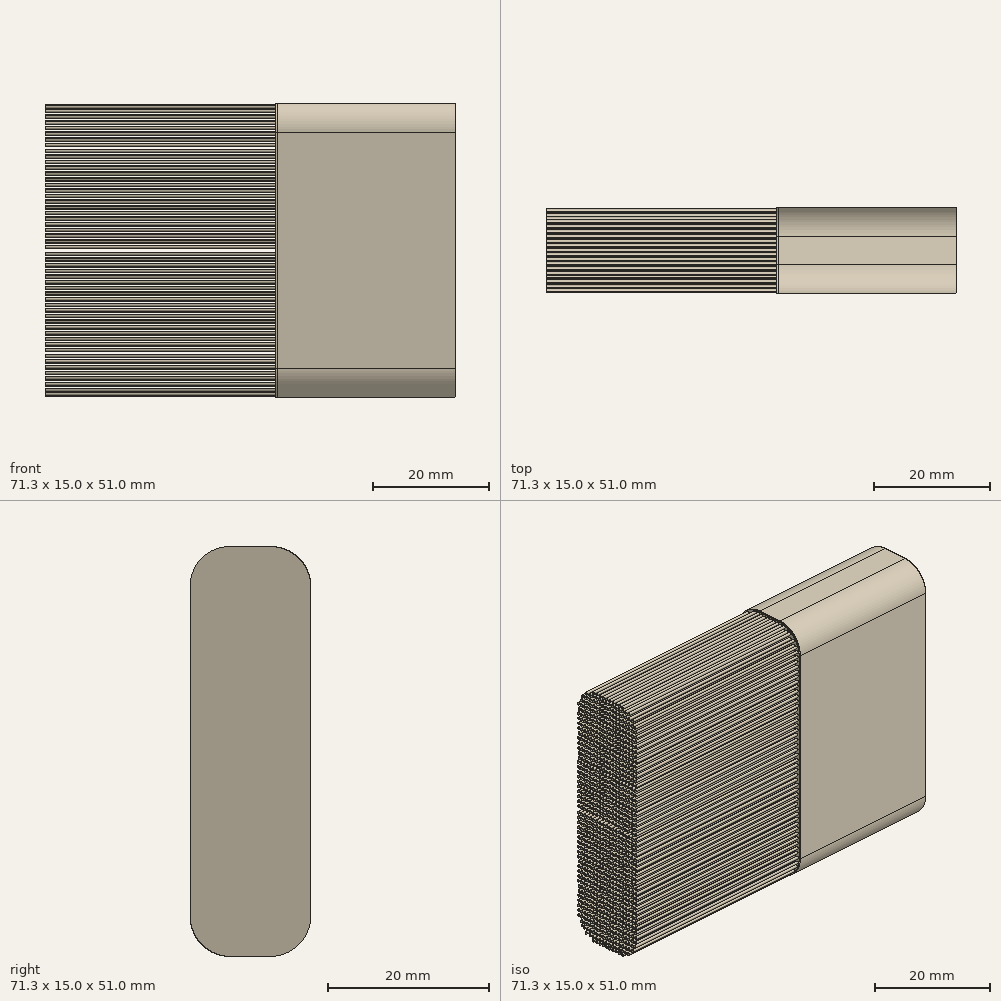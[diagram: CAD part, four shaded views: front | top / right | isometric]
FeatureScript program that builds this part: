
annotation { "Feature Type Name" : "Feature", "Feature Type Description" : "" }
export const myFeature = defineFeature(function(context is Context, id is Id, definition is map)
    precondition{}
    {
        {
            var Q0;
            Q0=qCreatedBy(makeId("Front.planeOp"),FACE);
            var sketch = newSketch(context, id + "F0", { "sketchPlane" : qUnion([Q0])});
            skLineSegment(sketch, "E0.bottom", {"start": v(15.5, -25.5) * mm, "end": v(-15.5, -25.5) * mm});
            skLineSegment(sketch, "E0.top", {"start": v(15.5, 25.5) * mm, "end": v(-15.5, 25.5) * mm});
            skLineSegment(sketch, "E0.left", {"start": v(15.5, -25.5) * mm, "end": v(15.5, 25.5) * mm});
            skLineSegment(sketch, "E0.right", {"start": v(-15.5, -25.5) * mm, "end": v(-15.5, 25.5) * mm});
            skPoint(sketch, "E0.middle", {"position": v(0, 0) * mm});
            skSolve(sketch);
        }
        {
            var Q0;
            Q0=makeQuery(id+"F0.imprint","IMPRINT",FACE,{"disambiguationData":[TD([[makeQuery(id+"F0.imprint","IMPRINT",EDGE,{"derivedFrom":sQuery(id+"F0.wireOp",EDGE,"E0.bottom")}),-1.0]])]});
            extrude(context, id + "F1", {"entities" : qUnion([Q0]), "depth" : 15 * mm});
        }
        {
            var Q0;
            Q0=makeQuery(id+"F1.opExtrude","CAP_EDGE",EDGE,{"disambiguationData":[OSD([sQuery(id+"F0.wireOp",EDGE,"E0.top")])],"isStart":true});
            var Q1;
            Q1=makeQuery(id+"F1.opExtrude","CAP_EDGE",EDGE,{"disambiguationData":[OSD([sQuery(id+"F0.wireOp",EDGE,"E0.bottom")])],"isStart":true});
            var Q2;
            Q2=makeQuery(id+"F1.opExtrude","CAP_EDGE",EDGE,{"disambiguationData":[OSD([sQuery(id+"F0.wireOp",EDGE,"E0.bottom")])],"isStart":false});
            var Q3;
            Q3=makeQuery(id+"F1.opExtrude","CAP_EDGE",EDGE,{"disambiguationData":[OSD([sQuery(id+"F0.wireOp",EDGE,"E0.top")])],"isStart":false});
            fillet(context, id + "F2", {"entities" : qUnion([Q0, Q1, Q2, Q3]), "radius" : 5 * mm, "tangentPropagation" : true, "allowEdgeOverflow" : false});
        }
        {
            var Q0;
            Q0=qCreatedBy(makeId("Right.planeOp"),FACE);
            cPlane(context, id + "F3", {"entities" : qUnion([Q0]), "cplaneType" : CPlaneType.OFFSET, "offset" : 15.8 * mm, "oppositeDirection" : true, "width" : 150 * mm, "height" : 150 * mm});
        }
        {
            var Q0;
            Q0=qCreatedBy(id+"F3.planeOp",FACE);
            var sketch = newSketch(context, id + "F4", { "sketchPlane" : qUnion([Q0])});
            skLineSegment(sketch, "E1.0.0", {"start": v(-10, 25.5) * mm, "end": v(-5, 25.5) * mm});
            skArc(sketch, "E1.0.1", {"start": v(-5, 25.5) * mm, "mid": v(-1.46, 24.04) * mm, "end": v(0, 20.5) * mm});
            skLineSegment(sketch, "E1.0.2", {"start": v(0, 20.5) * mm, "end": v(0, -20.5) * mm});
            skArc(sketch, "E1.0.3", {"start": v(0, -20.5) * mm, "mid": v(-1.46, -24.04) * mm, "end": v(-5, -25.5) * mm});
            skLineSegment(sketch, "E1.0.4", {"start": v(-5, -25.5) * mm, "end": v(-10, -25.5) * mm});
            skArc(sketch, "E1.0.5", {"start": v(-10, -25.5) * mm, "mid": v(-13.54, -24.04) * mm, "end": v(-15, -20.5) * mm});
            skLineSegment(sketch, "E1.0.6", {"start": v(-15, -20.5) * mm, "end": v(-15, 20.5) * mm});
            skArc(sketch, "E1.0.7", {"start": v(-15, 20.5) * mm, "mid": v(-13.54, 24.04) * mm, "end": v(-10, 25.5) * mm});
            skSolve(sketch);
        }
        {
            var Q0;
            Q0=makeQuery(id+"F4.imprint","IMPRINT",FACE,{"disambiguationData":[TD([[makeQuery(id+"F4.imprint","IMPRINT",EDGE,{"derivedFrom":sQuery(id+"F4.wireOp",EDGE,"E1.0.0")}),-1.0]])]});
            extrude(context, id + "F5", {"entities" : qUnion([Q0]), "depth" : 0.3 * mm});
        }
        {
            var Q0;
            Q0=makeQuery(id+"F4.imprint","IMPRINT",FACE,{"disambiguationData":[TD([[makeQuery(id+"F4.imprint","IMPRINT",EDGE,{"derivedFrom":sQuery(id+"F4.wireOp",EDGE,"E1.0.0")}),-1.0]])]});
            var sketch = newSketch(context, id + "F6", { "sketchPlane" : qUnion([Q0])});
            skCircle(sketch, "E2", {"center": v(-8.78, 4.59) * mm, "radius": 0.25 * mm});
            skCircle(sketch, "E3", {"center": v(-9.57, 4.53) * mm, "radius": 0.25 * mm});
            skCircle(sketch, "E4", {"center": v(-10.4, 4.5) * mm, "radius": 0.25 * mm});
            skCircle(sketch, "E5", {"center": v(-11.22, 4.53) * mm, "radius": 0.25 * mm});
            skCircle(sketch, "E6", {"center": v(-8, 4.59) * mm, "radius": 0.25 * mm});
            skCircle(sketch, "E7", {"center": v(-13.64, 4.5) * mm, "radius": 0.25 * mm});
            skCircle(sketch, "E8", {"center": v(-11.98, 4.56) * mm, "radius": 0.25 * mm});
            skCircle(sketch, "E9", {"center": v(-14.45, 4.53) * mm, "radius": 0.25 * mm});
            skCircle(sketch, "E10", {"center": v(-0.37, 4.62) * mm, "radius": 0.25 * mm});
            skCircle(sketch, "E11", {"center": v(-12.74, 4.5) * mm, "radius": 0.25 * mm});
            skCircle(sketch, "E12", {"center": v(-6.43, 4.55) * mm, "radius": 0.25 * mm});
            skCircle(sketch, "E13", {"center": v(-5.64, 4.6) * mm, "radius": 0.25 * mm});
            skCircle(sketch, "E14", {"center": v(-4.8, 4.63) * mm, "radius": 0.25 * mm});
            skCircle(sketch, "E15", {"center": v(-3.99, 4.6) * mm, "radius": 0.25 * mm});
            skCircle(sketch, "E16", {"center": v(-7.22, 4.55) * mm, "radius": 0.25 * mm});
            skCircle(sketch, "E17", {"center": v(-1.78, 4.61) * mm, "radius": 0.25 * mm});
            skCircle(sketch, "E18", {"center": v(-3.23, 4.58) * mm, "radius": 0.25 * mm});
            skCircle(sketch, "E19", {"center": v(-1.03, 4.63) * mm, "radius": 0.25 * mm});
            skCircle(sketch, "E20", {"center": v(-2.47, 4.63) * mm, "radius": 0.25 * mm});
            skCircle(sketch, "E21", {"center": v(-8.86, 3.61) * mm, "radius": 0.25 * mm});
            skCircle(sketch, "E22", {"center": v(-9.64, 3.56) * mm, "radius": 0.25 * mm});
            skCircle(sketch, "E23", {"center": v(-10.48, 3.53) * mm, "radius": 0.25 * mm});
            skCircle(sketch, "E24", {"center": v(-11.3, 3.56) * mm, "radius": 0.25 * mm});
            skCircle(sketch, "E25", {"center": v(-8.07, 3.61) * mm, "radius": 0.25 * mm});
            skCircle(sketch, "E26", {"center": v(-13.71, 3.53) * mm, "radius": 0.25 * mm});
            skCircle(sketch, "E27", {"center": v(-12.06, 3.59) * mm, "radius": 0.25 * mm});
            skCircle(sketch, "E28", {"center": v(-14.52, 3.56) * mm, "radius": 0.25 * mm});
            skCircle(sketch, "E29", {"center": v(-0.44, 3.65) * mm, "radius": 0.25 * mm});
            skCircle(sketch, "E30", {"center": v(-12.82, 3.53) * mm, "radius": 0.25 * mm});
            skCircle(sketch, "E31", {"center": v(-6.5, 3.58) * mm, "radius": 0.25 * mm});
            skCircle(sketch, "E32", {"center": v(-5.72, 3.63) * mm, "radius": 0.25 * mm});
            skCircle(sketch, "E33", {"center": v(-4.88, 3.66) * mm, "radius": 0.25 * mm});
            skCircle(sketch, "E34", {"center": v(-4.06, 3.63) * mm, "radius": 0.25 * mm});
            skCircle(sketch, "E35", {"center": v(-7.3, 3.58) * mm, "radius": 0.25 * mm});
            skCircle(sketch, "E36", {"center": v(-1.86, 3.64) * mm, "radius": 0.25 * mm});
            skCircle(sketch, "E37", {"center": v(-3.3, 3.6) * mm, "radius": 0.25 * mm});
            skCircle(sketch, "E38", {"center": v(-1.1, 3.66) * mm, "radius": 0.25 * mm});
            skCircle(sketch, "E39", {"center": v(-2.54, 3.66) * mm, "radius": 0.25 * mm});
            skCircle(sketch, "E40", {"center": v(-8.86, 2.59) * mm, "radius": 0.25 * mm});
            skCircle(sketch, "E41", {"center": v(-9.64, 2.54) * mm, "radius": 0.25 * mm});
            skCircle(sketch, "E42", {"center": v(-10.48, 2.51) * mm, "radius": 0.25 * mm});
            skCircle(sketch, "E43", {"center": v(-11.3, 2.54) * mm, "radius": 0.25 * mm});
            skCircle(sketch, "E44", {"center": v(-8.07, 2.59) * mm, "radius": 0.25 * mm});
            skCircle(sketch, "E45", {"center": v(-13.71, 2.51) * mm, "radius": 0.25 * mm});
            skCircle(sketch, "E46", {"center": v(-12.06, 2.56) * mm, "radius": 0.25 * mm});
            skCircle(sketch, "E47", {"center": v(-14.52, 2.54) * mm, "radius": 0.25 * mm});
            skCircle(sketch, "E48", {"center": v(-0.44, 2.63) * mm, "radius": 0.25 * mm});
            skCircle(sketch, "E49", {"center": v(-12.82, 2.51) * mm, "radius": 0.25 * mm});
            skCircle(sketch, "E50", {"center": v(-6.5, 2.56) * mm, "radius": 0.25 * mm});
            skCircle(sketch, "E51", {"center": v(-5.72, 2.6) * mm, "radius": 0.25 * mm});
            skCircle(sketch, "E52", {"center": v(-4.88, 2.64) * mm, "radius": 0.25 * mm});
            skCircle(sketch, "E53", {"center": v(-4.06, 2.6) * mm, "radius": 0.25 * mm});
            skCircle(sketch, "E54", {"center": v(-7.3, 2.56) * mm, "radius": 0.25 * mm});
            skCircle(sketch, "E55", {"center": v(-1.86, 2.62) * mm, "radius": 0.25 * mm});
            skCircle(sketch, "E56", {"center": v(-3.3, 2.58) * mm, "radius": 0.25 * mm});
            skCircle(sketch, "E57", {"center": v(-1.1, 2.64) * mm, "radius": 0.25 * mm});
            skCircle(sketch, "E58", {"center": v(-2.54, 2.64) * mm, "radius": 0.25 * mm});
            skCircle(sketch, "E59", {"center": v(-8.86, 1.62) * mm, "radius": 0.25 * mm});
            skCircle(sketch, "E60", {"center": v(-9.64, 1.56) * mm, "radius": 0.25 * mm});
            skCircle(sketch, "E61", {"center": v(-10.48, 1.54) * mm, "radius": 0.25 * mm});
            skCircle(sketch, "E62", {"center": v(-11.3, 1.56) * mm, "radius": 0.25 * mm});
            skCircle(sketch, "E63", {"center": v(-8.07, 1.62) * mm, "radius": 0.25 * mm});
            skCircle(sketch, "E64", {"center": v(-13.71, 1.54) * mm, "radius": 0.25 * mm});
            skCircle(sketch, "E65", {"center": v(-12.06, 1.6) * mm, "radius": 0.25 * mm});
            skCircle(sketch, "E66", {"center": v(-14.52, 1.56) * mm, "radius": 0.25 * mm});
            skCircle(sketch, "E67", {"center": v(-0.44, 1.65) * mm, "radius": 0.25 * mm});
            skCircle(sketch, "E68", {"center": v(-12.82, 1.54) * mm, "radius": 0.25 * mm});
            skCircle(sketch, "E69", {"center": v(-6.5, 1.58) * mm, "radius": 0.25 * mm});
            skCircle(sketch, "E70", {"center": v(-5.72, 1.64) * mm, "radius": 0.25 * mm});
            skCircle(sketch, "E71", {"center": v(-4.88, 1.66) * mm, "radius": 0.25 * mm});
            skCircle(sketch, "E72", {"center": v(-4.06, 1.64) * mm, "radius": 0.25 * mm});
            skCircle(sketch, "E73", {"center": v(-7.3, 1.58) * mm, "radius": 0.25 * mm});
            skCircle(sketch, "E74", {"center": v(-1.86, 1.64) * mm, "radius": 0.25 * mm});
            skCircle(sketch, "E75", {"center": v(-3.3, 1.61) * mm, "radius": 0.25 * mm});
            skCircle(sketch, "E76", {"center": v(-1.1, 1.66) * mm, "radius": 0.25 * mm});
            skCircle(sketch, "E77", {"center": v(-2.54, 1.66) * mm, "radius": 0.25 * mm});
            skCircle(sketch, "E78", {"center": v(-8.9, 0.62) * mm, "radius": 0.25 * mm});
            skCircle(sketch, "E79", {"center": v(-9.69, 0.57) * mm, "radius": 0.25 * mm});
            skCircle(sketch, "E80", {"center": v(-10.52, 0.54) * mm, "radius": 0.25 * mm});
            skCircle(sketch, "E81", {"center": v(-11.34, 0.57) * mm, "radius": 0.25 * mm});
            skCircle(sketch, "E82", {"center": v(-8.11, 0.62) * mm, "radius": 0.25 * mm});
            skCircle(sketch, "E83", {"center": v(-13.75, 0.54) * mm, "radius": 0.25 * mm});
            skCircle(sketch, "E84", {"center": v(-12.1, 0.6) * mm, "radius": 0.25 * mm});
            skCircle(sketch, "E85", {"center": v(-14.57, 0.57) * mm, "radius": 0.25 * mm});
            skCircle(sketch, "E86", {"center": v(-0.49, 0.66) * mm, "radius": 0.25 * mm});
            skCircle(sketch, "E87", {"center": v(-12.86, 0.54) * mm, "radius": 0.25 * mm});
            skCircle(sketch, "E88", {"center": v(-6.55, 0.6) * mm, "radius": 0.25 * mm});
            skCircle(sketch, "E89", {"center": v(-5.76, 0.64) * mm, "radius": 0.25 * mm});
            skCircle(sketch, "E90", {"center": v(-4.92, 0.67) * mm, "radius": 0.25 * mm});
            skCircle(sketch, "E91", {"center": v(-4.1, 0.64) * mm, "radius": 0.25 * mm});
            skCircle(sketch, "E92", {"center": v(-7.33, 0.6) * mm, "radius": 0.25 * mm});
            skCircle(sketch, "E93", {"center": v(-1.9, 0.65) * mm, "radius": 0.25 * mm});
            skCircle(sketch, "E94", {"center": v(-3.34, 0.62) * mm, "radius": 0.25 * mm});
            skCircle(sketch, "E95", {"center": v(-1.14, 0.67) * mm, "radius": 0.25 * mm});
            skCircle(sketch, "E96", {"center": v(-2.58, 0.67) * mm, "radius": 0.25 * mm});
            skCircle(sketch, "E97", {"center": v(-8.78, 9.52) * mm, "radius": 0.25 * mm});
            skCircle(sketch, "E98", {"center": v(-9.57, 9.47) * mm, "radius": 0.25 * mm});
            skCircle(sketch, "E99", {"center": v(-10.4, 9.44) * mm, "radius": 0.25 * mm});
            skCircle(sketch, "E100", {"center": v(-11.22, 9.47) * mm, "radius": 0.25 * mm});
            skCircle(sketch, "E101", {"center": v(-8, 9.52) * mm, "radius": 0.25 * mm});
            skCircle(sketch, "E102", {"center": v(-13.64, 9.44) * mm, "radius": 0.25 * mm});
            skCircle(sketch, "E103", {"center": v(-11.98, 9.5) * mm, "radius": 0.25 * mm});
            skCircle(sketch, "E104", {"center": v(-14.45, 9.47) * mm, "radius": 0.25 * mm});
            skCircle(sketch, "E105", {"center": v(-0.37, 9.56) * mm, "radius": 0.25 * mm});
            skCircle(sketch, "E106", {"center": v(-12.74, 9.44) * mm, "radius": 0.25 * mm});
            skCircle(sketch, "E107", {"center": v(-6.43, 9.5) * mm, "radius": 0.25 * mm});
            skCircle(sketch, "E108", {"center": v(-5.64, 9.54) * mm, "radius": 0.25 * mm});
            skCircle(sketch, "E109", {"center": v(-4.8, 9.57) * mm, "radius": 0.25 * mm});
            skCircle(sketch, "E110", {"center": v(-3.99, 9.54) * mm, "radius": 0.25 * mm});
            skCircle(sketch, "E111", {"center": v(-7.22, 9.5) * mm, "radius": 0.25 * mm});
            skCircle(sketch, "E112", {"center": v(-1.78, 9.55) * mm, "radius": 0.25 * mm});
            skCircle(sketch, "E113", {"center": v(-3.23, 9.52) * mm, "radius": 0.25 * mm});
            skCircle(sketch, "E114", {"center": v(-1.03, 9.57) * mm, "radius": 0.25 * mm});
            skCircle(sketch, "E115", {"center": v(-2.47, 9.57) * mm, "radius": 0.25 * mm});
            skCircle(sketch, "E116", {"center": v(-8.86, 8.55) * mm, "radius": 0.25 * mm});
            skCircle(sketch, "E117", {"center": v(-9.64, 8.5) * mm, "radius": 0.25 * mm});
            skCircle(sketch, "E118", {"center": v(-10.48, 8.47) * mm, "radius": 0.25 * mm});
            skCircle(sketch, "E119", {"center": v(-11.3, 8.5) * mm, "radius": 0.25 * mm});
            skCircle(sketch, "E120", {"center": v(-8.07, 8.55) * mm, "radius": 0.25 * mm});
            skCircle(sketch, "E121", {"center": v(-13.71, 8.47) * mm, "radius": 0.25 * mm});
            skCircle(sketch, "E122", {"center": v(-12.06, 8.52) * mm, "radius": 0.25 * mm});
            skCircle(sketch, "E123", {"center": v(-14.52, 8.5) * mm, "radius": 0.25 * mm});
            skCircle(sketch, "E124", {"center": v(-0.44, 8.59) * mm, "radius": 0.25 * mm});
            skCircle(sketch, "E125", {"center": v(-12.82, 8.47) * mm, "radius": 0.25 * mm});
            skCircle(sketch, "E126", {"center": v(-6.5, 8.52) * mm, "radius": 0.25 * mm});
            skCircle(sketch, "E127", {"center": v(-5.72, 8.57) * mm, "radius": 0.25 * mm});
            skCircle(sketch, "E128", {"center": v(-4.88, 8.6) * mm, "radius": 0.25 * mm});
            skCircle(sketch, "E129", {"center": v(-4.06, 8.57) * mm, "radius": 0.25 * mm});
            skCircle(sketch, "E130", {"center": v(-7.3, 8.52) * mm, "radius": 0.25 * mm});
            skCircle(sketch, "E131", {"center": v(-1.86, 8.58) * mm, "radius": 0.25 * mm});
            skCircle(sketch, "E132", {"center": v(-3.3, 8.54) * mm, "radius": 0.25 * mm});
            skCircle(sketch, "E133", {"center": v(-1.1, 8.6) * mm, "radius": 0.25 * mm});
            skCircle(sketch, "E134", {"center": v(-2.54, 8.6) * mm, "radius": 0.25 * mm});
            skCircle(sketch, "E135", {"center": v(-8.86, 7.53) * mm, "radius": 0.25 * mm});
            skCircle(sketch, "E136", {"center": v(-9.64, 7.47) * mm, "radius": 0.25 * mm});
            skCircle(sketch, "E137", {"center": v(-10.48, 7.45) * mm, "radius": 0.25 * mm});
            skCircle(sketch, "E138", {"center": v(-11.3, 7.47) * mm, "radius": 0.25 * mm});
            skCircle(sketch, "E139", {"center": v(-8.07, 7.53) * mm, "radius": 0.25 * mm});
            skCircle(sketch, "E140", {"center": v(-13.71, 7.45) * mm, "radius": 0.25 * mm});
            skCircle(sketch, "E141", {"center": v(-12.06, 7.5) * mm, "radius": 0.25 * mm});
            skCircle(sketch, "E142", {"center": v(-14.52, 7.47) * mm, "radius": 0.25 * mm});
            skCircle(sketch, "E143", {"center": v(-0.44, 7.56) * mm, "radius": 0.25 * mm});
            skCircle(sketch, "E144", {"center": v(-12.82, 7.45) * mm, "radius": 0.25 * mm});
            skCircle(sketch, "E145", {"center": v(-6.5, 7.5) * mm, "radius": 0.25 * mm});
            skCircle(sketch, "E146", {"center": v(-5.72, 7.55) * mm, "radius": 0.25 * mm});
            skCircle(sketch, "E147", {"center": v(-4.88, 7.57) * mm, "radius": 0.25 * mm});
            skCircle(sketch, "E148", {"center": v(-4.06, 7.55) * mm, "radius": 0.25 * mm});
            skCircle(sketch, "E149", {"center": v(-7.3, 7.5) * mm, "radius": 0.25 * mm});
            skCircle(sketch, "E150", {"center": v(-1.86, 7.55) * mm, "radius": 0.25 * mm});
            skCircle(sketch, "E151", {"center": v(-3.3, 7.52) * mm, "radius": 0.25 * mm});
            skCircle(sketch, "E152", {"center": v(-1.1, 7.57) * mm, "radius": 0.25 * mm});
            skCircle(sketch, "E153", {"center": v(-2.54, 7.57) * mm, "radius": 0.25 * mm});
            skCircle(sketch, "E154", {"center": v(-8.86, 6.55) * mm, "radius": 0.25 * mm});
            skCircle(sketch, "E155", {"center": v(-9.64, 6.5) * mm, "radius": 0.25 * mm});
            skCircle(sketch, "E156", {"center": v(-10.48, 6.47) * mm, "radius": 0.25 * mm});
            skCircle(sketch, "E157", {"center": v(-11.3, 6.5) * mm, "radius": 0.25 * mm});
            skCircle(sketch, "E158", {"center": v(-8.07, 6.55) * mm, "radius": 0.25 * mm});
            skCircle(sketch, "E159", {"center": v(-13.71, 6.47) * mm, "radius": 0.25 * mm});
            skCircle(sketch, "E160", {"center": v(-12.06, 6.53) * mm, "radius": 0.25 * mm});
            skCircle(sketch, "E161", {"center": v(-14.52, 6.5) * mm, "radius": 0.25 * mm});
            skCircle(sketch, "E162", {"center": v(-0.44, 6.6) * mm, "radius": 0.25 * mm});
            skCircle(sketch, "E163", {"center": v(-12.82, 6.47) * mm, "radius": 0.25 * mm});
            skCircle(sketch, "E164", {"center": v(-6.5, 6.52) * mm, "radius": 0.25 * mm});
            skCircle(sketch, "E165", {"center": v(-5.72, 6.57) * mm, "radius": 0.25 * mm});
            skCircle(sketch, "E166", {"center": v(-4.88, 6.6) * mm, "radius": 0.25 * mm});
            skCircle(sketch, "E167", {"center": v(-4.06, 6.57) * mm, "radius": 0.25 * mm});
            skCircle(sketch, "E168", {"center": v(-7.3, 6.52) * mm, "radius": 0.25 * mm});
            skCircle(sketch, "E169", {"center": v(-1.86, 6.58) * mm, "radius": 0.25 * mm});
            skCircle(sketch, "E170", {"center": v(-3.3, 6.55) * mm, "radius": 0.25 * mm});
            skCircle(sketch, "E171", {"center": v(-1.1, 6.6) * mm, "radius": 0.25 * mm});
            skCircle(sketch, "E172", {"center": v(-2.54, 6.6) * mm, "radius": 0.25 * mm});
            skCircle(sketch, "E173", {"center": v(-8.9, 5.56) * mm, "radius": 0.25 * mm});
            skCircle(sketch, "E174", {"center": v(-9.69, 5.5) * mm, "radius": 0.25 * mm});
            skCircle(sketch, "E175", {"center": v(-10.52, 5.48) * mm, "radius": 0.25 * mm});
            skCircle(sketch, "E176", {"center": v(-11.34, 5.5) * mm, "radius": 0.25 * mm});
            skCircle(sketch, "E177", {"center": v(-8.11, 5.56) * mm, "radius": 0.25 * mm});
            skCircle(sketch, "E178", {"center": v(-13.75, 5.48) * mm, "radius": 0.25 * mm});
            skCircle(sketch, "E179", {"center": v(-12.1, 5.53) * mm, "radius": 0.25 * mm});
            skCircle(sketch, "E180", {"center": v(-14.57, 5.5) * mm, "radius": 0.25 * mm});
            skCircle(sketch, "E181", {"center": v(-0.49, 5.6) * mm, "radius": 0.25 * mm});
            skCircle(sketch, "E182", {"center": v(-12.86, 5.48) * mm, "radius": 0.25 * mm});
            skCircle(sketch, "E183", {"center": v(-6.55, 5.53) * mm, "radius": 0.25 * mm});
            skCircle(sketch, "E184", {"center": v(-5.76, 5.58) * mm, "radius": 0.25 * mm});
            skCircle(sketch, "E185", {"center": v(-4.92, 5.6) * mm, "radius": 0.25 * mm});
            skCircle(sketch, "E186", {"center": v(-4.1, 5.58) * mm, "radius": 0.25 * mm});
            skCircle(sketch, "E187", {"center": v(-7.33, 5.53) * mm, "radius": 0.25 * mm});
            skCircle(sketch, "E188", {"center": v(-1.9, 5.59) * mm, "radius": 0.25 * mm});
            skCircle(sketch, "E189", {"center": v(-3.34, 5.55) * mm, "radius": 0.25 * mm});
            skCircle(sketch, "E190", {"center": v(-1.14, 5.6) * mm, "radius": 0.25 * mm});
            skCircle(sketch, "E191", {"center": v(-2.58, 5.6) * mm, "radius": 0.25 * mm});
            skCircle(sketch, "E192", {"center": v(-8.86, 14.4) * mm, "radius": 0.25 * mm});
            skCircle(sketch, "E193", {"center": v(-9.64, 14.35) * mm, "radius": 0.25 * mm});
            skCircle(sketch, "E194", {"center": v(-10.48, 14.32) * mm, "radius": 0.25 * mm});
            skCircle(sketch, "E195", {"center": v(-11.3, 14.35) * mm, "radius": 0.25 * mm});
            skCircle(sketch, "E196", {"center": v(-8.07, 14.4) * mm, "radius": 0.25 * mm});
            skCircle(sketch, "E197", {"center": v(-13.71, 14.32) * mm, "radius": 0.25 * mm});
            skCircle(sketch, "E198", {"center": v(-12.06, 14.38) * mm, "radius": 0.25 * mm});
            skCircle(sketch, "E199", {"center": v(-14.52, 14.35) * mm, "radius": 0.25 * mm});
            skCircle(sketch, "E200", {"center": v(-0.44, 14.44) * mm, "radius": 0.25 * mm});
            skCircle(sketch, "E201", {"center": v(-12.82, 14.32) * mm, "radius": 0.25 * mm});
            skCircle(sketch, "E202", {"center": v(-6.5, 14.37) * mm, "radius": 0.25 * mm});
            skCircle(sketch, "E203", {"center": v(-5.72, 14.42) * mm, "radius": 0.25 * mm});
            skCircle(sketch, "E204", {"center": v(-4.88, 14.45) * mm, "radius": 0.25 * mm});
            skCircle(sketch, "E205", {"center": v(-4.06, 14.42) * mm, "radius": 0.25 * mm});
            skCircle(sketch, "E206", {"center": v(-7.3, 14.37) * mm, "radius": 0.25 * mm});
            skCircle(sketch, "E207", {"center": v(-1.86, 14.43) * mm, "radius": 0.25 * mm});
            skCircle(sketch, "E208", {"center": v(-3.3, 14.4) * mm, "radius": 0.25 * mm});
            skCircle(sketch, "E209", {"center": v(-1.1, 14.45) * mm, "radius": 0.25 * mm});
            skCircle(sketch, "E210", {"center": v(-2.54, 14.45) * mm, "radius": 0.25 * mm});
            skCircle(sketch, "E211", {"center": v(-8.93, 13.43) * mm, "radius": 0.25 * mm});
            skCircle(sketch, "E212", {"center": v(-9.72, 13.38) * mm, "radius": 0.25 * mm});
            skCircle(sketch, "E213", {"center": v(-10.56, 13.35) * mm, "radius": 0.25 * mm});
            skCircle(sketch, "E214", {"center": v(-11.37, 13.38) * mm, "radius": 0.25 * mm});
            skCircle(sketch, "E215", {"center": v(-8.14, 13.43) * mm, "radius": 0.25 * mm});
            skCircle(sketch, "E216", {"center": v(-13.79, 13.35) * mm, "radius": 0.25 * mm});
            skCircle(sketch, "E217", {"center": v(-12.13, 13.4) * mm, "radius": 0.25 * mm});
            skCircle(sketch, "E218", {"center": v(-14.6, 13.38) * mm, "radius": 0.25 * mm});
            skCircle(sketch, "E219", {"center": v(-0.52, 13.46) * mm, "radius": 0.25 * mm});
            skCircle(sketch, "E220", {"center": v(-12.9, 13.35) * mm, "radius": 0.25 * mm});
            skCircle(sketch, "E221", {"center": v(-6.58, 13.4) * mm, "radius": 0.25 * mm});
            skCircle(sketch, "E222", {"center": v(-5.8, 13.45) * mm, "radius": 0.25 * mm});
            skCircle(sketch, "E223", {"center": v(-4.95, 13.47) * mm, "radius": 0.25 * mm});
            skCircle(sketch, "E224", {"center": v(-4.14, 13.45) * mm, "radius": 0.25 * mm});
            skCircle(sketch, "E225", {"center": v(-7.37, 13.4) * mm, "radius": 0.25 * mm});
            skCircle(sketch, "E226", {"center": v(-1.93, 13.46) * mm, "radius": 0.25 * mm});
            skCircle(sketch, "E227", {"center": v(-3.38, 13.42) * mm, "radius": 0.25 * mm});
            skCircle(sketch, "E228", {"center": v(-1.18, 13.47) * mm, "radius": 0.25 * mm});
            skCircle(sketch, "E229", {"center": v(-2.62, 13.47) * mm, "radius": 0.25 * mm});
            skCircle(sketch, "E230", {"center": v(-8.93, 12.4) * mm, "radius": 0.25 * mm});
            skCircle(sketch, "E231", {"center": v(-9.72, 12.35) * mm, "radius": 0.25 * mm});
            skCircle(sketch, "E232", {"center": v(-10.56, 12.33) * mm, "radius": 0.25 * mm});
            skCircle(sketch, "E233", {"center": v(-11.37, 12.35) * mm, "radius": 0.25 * mm});
            skCircle(sketch, "E234", {"center": v(-8.14, 12.4) * mm, "radius": 0.25 * mm});
            skCircle(sketch, "E235", {"center": v(-13.79, 12.33) * mm, "radius": 0.25 * mm});
            skCircle(sketch, "E236", {"center": v(-12.13, 12.38) * mm, "radius": 0.25 * mm});
            skCircle(sketch, "E237", {"center": v(-14.6, 12.35) * mm, "radius": 0.25 * mm});
            skCircle(sketch, "E238", {"center": v(-0.52, 12.44) * mm, "radius": 0.25 * mm});
            skCircle(sketch, "E239", {"center": v(-12.9, 12.33) * mm, "radius": 0.25 * mm});
            skCircle(sketch, "E240", {"center": v(-6.58, 12.37) * mm, "radius": 0.25 * mm});
            skCircle(sketch, "E241", {"center": v(-5.8, 12.43) * mm, "radius": 0.25 * mm});
            skCircle(sketch, "E242", {"center": v(-4.95, 12.45) * mm, "radius": 0.25 * mm});
            skCircle(sketch, "E243", {"center": v(-4.14, 12.43) * mm, "radius": 0.25 * mm});
            skCircle(sketch, "E244", {"center": v(-7.37, 12.37) * mm, "radius": 0.25 * mm});
            skCircle(sketch, "E245", {"center": v(-1.93, 12.43) * mm, "radius": 0.25 * mm});
            skCircle(sketch, "E246", {"center": v(-3.38, 12.4) * mm, "radius": 0.25 * mm});
            skCircle(sketch, "E247", {"center": v(-1.18, 12.45) * mm, "radius": 0.25 * mm});
            skCircle(sketch, "E248", {"center": v(-2.62, 12.45) * mm, "radius": 0.25 * mm});
            skCircle(sketch, "E249", {"center": v(-8.93, 11.43) * mm, "radius": 0.25 * mm});
            skCircle(sketch, "E250", {"center": v(-9.72, 11.38) * mm, "radius": 0.25 * mm});
            skCircle(sketch, "E251", {"center": v(-10.56, 11.35) * mm, "radius": 0.25 * mm});
            skCircle(sketch, "E252", {"center": v(-11.37, 11.38) * mm, "radius": 0.25 * mm});
            skCircle(sketch, "E253", {"center": v(-8.14, 11.43) * mm, "radius": 0.25 * mm});
            skCircle(sketch, "E254", {"center": v(-13.79, 11.35) * mm, "radius": 0.25 * mm});
            skCircle(sketch, "E255", {"center": v(-12.13, 11.4) * mm, "radius": 0.25 * mm});
            skCircle(sketch, "E256", {"center": v(-14.6, 11.38) * mm, "radius": 0.25 * mm});
            skCircle(sketch, "E257", {"center": v(-0.52, 11.47) * mm, "radius": 0.25 * mm});
            skCircle(sketch, "E258", {"center": v(-12.9, 11.35) * mm, "radius": 0.25 * mm});
            skCircle(sketch, "E259", {"center": v(-6.58, 11.4) * mm, "radius": 0.25 * mm});
            skCircle(sketch, "E260", {"center": v(-5.8, 11.45) * mm, "radius": 0.25 * mm});
            skCircle(sketch, "E261", {"center": v(-4.95, 11.48) * mm, "radius": 0.25 * mm});
            skCircle(sketch, "E262", {"center": v(-4.14, 11.45) * mm, "radius": 0.25 * mm});
            skCircle(sketch, "E263", {"center": v(-7.37, 11.4) * mm, "radius": 0.25 * mm});
            skCircle(sketch, "E264", {"center": v(-1.93, 11.46) * mm, "radius": 0.25 * mm});
            skCircle(sketch, "E265", {"center": v(-3.38, 11.43) * mm, "radius": 0.25 * mm});
            skCircle(sketch, "E266", {"center": v(-1.18, 11.48) * mm, "radius": 0.25 * mm});
            skCircle(sketch, "E267", {"center": v(-2.62, 11.48) * mm, "radius": 0.25 * mm});
            skCircle(sketch, "E268", {"center": v(-8.97, 10.44) * mm, "radius": 0.25 * mm});
            skCircle(sketch, "E269", {"center": v(-9.76, 10.39) * mm, "radius": 0.25 * mm});
            skCircle(sketch, "E270", {"center": v(-10.6, 10.36) * mm, "radius": 0.25 * mm});
            skCircle(sketch, "E271", {"center": v(-11.41, 10.39) * mm, "radius": 0.25 * mm});
            skCircle(sketch, "E272", {"center": v(-8.19, 10.44) * mm, "radius": 0.25 * mm});
            skCircle(sketch, "E273", {"center": v(-13.83, 10.36) * mm, "radius": 0.25 * mm});
            skCircle(sketch, "E274", {"center": v(-12.17, 10.41) * mm, "radius": 0.25 * mm});
            skCircle(sketch, "E275", {"center": v(-14.64, 10.39) * mm, "radius": 0.25 * mm});
            skCircle(sketch, "E276", {"center": v(-0.56, 10.48) * mm, "radius": 0.25 * mm});
            skCircle(sketch, "E277", {"center": v(-12.94, 10.36) * mm, "radius": 0.25 * mm});
            skCircle(sketch, "E278", {"center": v(-6.62, 10.4) * mm, "radius": 0.25 * mm});
            skCircle(sketch, "E279", {"center": v(-5.83, 10.46) * mm, "radius": 0.25 * mm});
            skCircle(sketch, "E280", {"center": v(-5, 10.49) * mm, "radius": 0.25 * mm});
            skCircle(sketch, "E281", {"center": v(-4.18, 10.46) * mm, "radius": 0.25 * mm});
            skCircle(sketch, "E282", {"center": v(-7.4, 10.4) * mm, "radius": 0.25 * mm});
            skCircle(sketch, "E283", {"center": v(-1.98, 10.47) * mm, "radius": 0.25 * mm});
            skCircle(sketch, "E284", {"center": v(-3.42, 10.43) * mm, "radius": 0.25 * mm});
            skCircle(sketch, "E285", {"center": v(-1.22, 10.49) * mm, "radius": 0.25 * mm});
            skCircle(sketch, "E286", {"center": v(-2.66, 10.49) * mm, "radius": 0.25 * mm});
            skCircle(sketch, "E287", {"center": v(-8.86, 19.34) * mm, "radius": 0.25 * mm});
            skCircle(sketch, "E288", {"center": v(-9.64, 19.29) * mm, "radius": 0.25 * mm});
            skCircle(sketch, "E289", {"center": v(-10.48, 19.26) * mm, "radius": 0.25 * mm});
            skCircle(sketch, "E290", {"center": v(-11.3, 19.29) * mm, "radius": 0.25 * mm});
            skCircle(sketch, "E291", {"center": v(-8.07, 19.34) * mm, "radius": 0.25 * mm});
            skCircle(sketch, "E292", {"center": v(-13.71, 19.26) * mm, "radius": 0.25 * mm});
            skCircle(sketch, "E293", {"center": v(-12.06, 19.31) * mm, "radius": 0.25 * mm});
            skCircle(sketch, "E294", {"center": v(-14.52, 19.29) * mm, "radius": 0.25 * mm});
            skCircle(sketch, "E295", {"center": v(-0.44, 19.38) * mm, "radius": 0.25 * mm});
            skCircle(sketch, "E296", {"center": v(-12.82, 19.26) * mm, "radius": 0.25 * mm});
            skCircle(sketch, "E297", {"center": v(-6.5, 19.3) * mm, "radius": 0.25 * mm});
            skCircle(sketch, "E298", {"center": v(-5.72, 19.36) * mm, "radius": 0.25 * mm});
            skCircle(sketch, "E299", {"center": v(-4.88, 19.39) * mm, "radius": 0.25 * mm});
            skCircle(sketch, "E300", {"center": v(-4.06, 19.36) * mm, "radius": 0.25 * mm});
            skCircle(sketch, "E301", {"center": v(-7.3, 19.3) * mm, "radius": 0.25 * mm});
            skCircle(sketch, "E302", {"center": v(-1.86, 19.37) * mm, "radius": 0.25 * mm});
            skCircle(sketch, "E303", {"center": v(-3.3, 19.33) * mm, "radius": 0.25 * mm});
            skCircle(sketch, "E304", {"center": v(-1.1, 19.39) * mm, "radius": 0.25 * mm});
            skCircle(sketch, "E305", {"center": v(-2.54, 19.39) * mm, "radius": 0.25 * mm});
            skCircle(sketch, "E306", {"center": v(-8.93, 18.36) * mm, "radius": 0.25 * mm});
            skCircle(sketch, "E307", {"center": v(-9.72, 18.31) * mm, "radius": 0.25 * mm});
            skCircle(sketch, "E308", {"center": v(-10.56, 18.29) * mm, "radius": 0.25 * mm});
            skCircle(sketch, "E309", {"center": v(-11.37, 18.31) * mm, "radius": 0.25 * mm});
            skCircle(sketch, "E310", {"center": v(-8.14, 18.36) * mm, "radius": 0.25 * mm});
            skCircle(sketch, "E311", {"center": v(-13.79, 18.29) * mm, "radius": 0.25 * mm});
            skCircle(sketch, "E312", {"center": v(-12.13, 18.34) * mm, "radius": 0.25 * mm});
            skCircle(sketch, "E313", {"center": v(-14.6, 18.31) * mm, "radius": 0.25 * mm});
            skCircle(sketch, "E314", {"center": v(-0.52, 18.4) * mm, "radius": 0.25 * mm});
            skCircle(sketch, "E315", {"center": v(-12.9, 18.29) * mm, "radius": 0.25 * mm});
            skCircle(sketch, "E316", {"center": v(-6.58, 18.33) * mm, "radius": 0.25 * mm});
            skCircle(sketch, "E317", {"center": v(-5.8, 18.38) * mm, "radius": 0.25 * mm});
            skCircle(sketch, "E318", {"center": v(-4.95, 18.41) * mm, "radius": 0.25 * mm});
            skCircle(sketch, "E319", {"center": v(-4.14, 18.38) * mm, "radius": 0.25 * mm});
            skCircle(sketch, "E320", {"center": v(-7.37, 18.33) * mm, "radius": 0.25 * mm});
            skCircle(sketch, "E321", {"center": v(-1.93, 18.4) * mm, "radius": 0.25 * mm});
            skCircle(sketch, "E322", {"center": v(-3.38, 18.36) * mm, "radius": 0.25 * mm});
            skCircle(sketch, "E323", {"center": v(-1.18, 18.41) * mm, "radius": 0.25 * mm});
            skCircle(sketch, "E324", {"center": v(-2.62, 18.41) * mm, "radius": 0.25 * mm});
            skCircle(sketch, "E325", {"center": v(-8.93, 17.34) * mm, "radius": 0.25 * mm});
            skCircle(sketch, "E326", {"center": v(-9.72, 17.29) * mm, "radius": 0.25 * mm});
            skCircle(sketch, "E327", {"center": v(-10.56, 17.26) * mm, "radius": 0.25 * mm});
            skCircle(sketch, "E328", {"center": v(-11.37, 17.29) * mm, "radius": 0.25 * mm});
            skCircle(sketch, "E329", {"center": v(-8.14, 17.34) * mm, "radius": 0.25 * mm});
            skCircle(sketch, "E330", {"center": v(-13.79, 17.26) * mm, "radius": 0.25 * mm});
            skCircle(sketch, "E331", {"center": v(-12.13, 17.32) * mm, "radius": 0.25 * mm});
            skCircle(sketch, "E332", {"center": v(-14.6, 17.29) * mm, "radius": 0.25 * mm});
            skCircle(sketch, "E333", {"center": v(-0.52, 17.38) * mm, "radius": 0.25 * mm});
            skCircle(sketch, "E334", {"center": v(-12.9, 17.26) * mm, "radius": 0.25 * mm});
            skCircle(sketch, "E335", {"center": v(-6.58, 17.31) * mm, "radius": 0.25 * mm});
            skCircle(sketch, "E336", {"center": v(-5.8, 17.36) * mm, "radius": 0.25 * mm});
            skCircle(sketch, "E337", {"center": v(-4.95, 17.39) * mm, "radius": 0.25 * mm});
            skCircle(sketch, "E338", {"center": v(-4.14, 17.36) * mm, "radius": 0.25 * mm});
            skCircle(sketch, "E339", {"center": v(-7.37, 17.31) * mm, "radius": 0.25 * mm});
            skCircle(sketch, "E340", {"center": v(-1.93, 17.37) * mm, "radius": 0.25 * mm});
            skCircle(sketch, "E341", {"center": v(-3.38, 17.34) * mm, "radius": 0.25 * mm});
            skCircle(sketch, "E342", {"center": v(-1.18, 17.39) * mm, "radius": 0.25 * mm});
            skCircle(sketch, "E343", {"center": v(-2.62, 17.39) * mm, "radius": 0.25 * mm});
            skCircle(sketch, "E344", {"center": v(-8.93, 16.37) * mm, "radius": 0.25 * mm});
            skCircle(sketch, "E345", {"center": v(-9.72, 16.32) * mm, "radius": 0.25 * mm});
            skCircle(sketch, "E346", {"center": v(-10.56, 16.3) * mm, "radius": 0.25 * mm});
            skCircle(sketch, "E347", {"center": v(-11.37, 16.32) * mm, "radius": 0.25 * mm});
            skCircle(sketch, "E348", {"center": v(-8.14, 16.37) * mm, "radius": 0.25 * mm});
            skCircle(sketch, "E349", {"center": v(-13.79, 16.3) * mm, "radius": 0.25 * mm});
            skCircle(sketch, "E350", {"center": v(-12.13, 16.34) * mm, "radius": 0.25 * mm});
            skCircle(sketch, "E351", {"center": v(-14.6, 16.32) * mm, "radius": 0.25 * mm});
            skCircle(sketch, "E352", {"center": v(-0.52, 16.4) * mm, "radius": 0.25 * mm});
            skCircle(sketch, "E353", {"center": v(-12.9, 16.3) * mm, "radius": 0.25 * mm});
            skCircle(sketch, "E354", {"center": v(-6.58, 16.34) * mm, "radius": 0.25 * mm});
            skCircle(sketch, "E355", {"center": v(-5.8, 16.4) * mm, "radius": 0.25 * mm});
            skCircle(sketch, "E356", {"center": v(-4.95, 16.42) * mm, "radius": 0.25 * mm});
            skCircle(sketch, "E357", {"center": v(-4.14, 16.4) * mm, "radius": 0.25 * mm});
            skCircle(sketch, "E358", {"center": v(-7.37, 16.34) * mm, "radius": 0.25 * mm});
            skCircle(sketch, "E359", {"center": v(-1.93, 16.4) * mm, "radius": 0.25 * mm});
            skCircle(sketch, "E360", {"center": v(-3.38, 16.36) * mm, "radius": 0.25 * mm});
            skCircle(sketch, "E361", {"center": v(-1.18, 16.42) * mm, "radius": 0.25 * mm});
            skCircle(sketch, "E362", {"center": v(-2.62, 16.42) * mm, "radius": 0.25 * mm});
            skCircle(sketch, "E363", {"center": v(-8.97, 15.38) * mm, "radius": 0.25 * mm});
            skCircle(sketch, "E364", {"center": v(-9.76, 15.32) * mm, "radius": 0.25 * mm});
            skCircle(sketch, "E365", {"center": v(-10.6, 15.3) * mm, "radius": 0.25 * mm});
            skCircle(sketch, "E366", {"center": v(-11.41, 15.32) * mm, "radius": 0.25 * mm});
            skCircle(sketch, "E367", {"center": v(-8.19, 15.38) * mm, "radius": 0.25 * mm});
            skCircle(sketch, "E368", {"center": v(-13.83, 15.3) * mm, "radius": 0.25 * mm});
            skCircle(sketch, "E369", {"center": v(-12.17, 15.35) * mm, "radius": 0.25 * mm});
            skCircle(sketch, "E370", {"center": v(-14.64, 15.32) * mm, "radius": 0.25 * mm});
            skCircle(sketch, "E371", {"center": v(-0.56, 15.41) * mm, "radius": 0.25 * mm});
            skCircle(sketch, "E372", {"center": v(-12.94, 15.3) * mm, "radius": 0.25 * mm});
            skCircle(sketch, "E373", {"center": v(-6.62, 15.34) * mm, "radius": 0.25 * mm});
            skCircle(sketch, "E374", {"center": v(-5.83, 15.4) * mm, "radius": 0.25 * mm});
            skCircle(sketch, "E375", {"center": v(-5, 15.42) * mm, "radius": 0.25 * mm});
            skCircle(sketch, "E376", {"center": v(-4.18, 15.4) * mm, "radius": 0.25 * mm});
            skCircle(sketch, "E377", {"center": v(-7.4, 15.34) * mm, "radius": 0.25 * mm});
            skCircle(sketch, "E378", {"center": v(-1.98, 15.4) * mm, "radius": 0.25 * mm});
            skCircle(sketch, "E379", {"center": v(-3.42, 15.37) * mm, "radius": 0.25 * mm});
            skCircle(sketch, "E380", {"center": v(-1.22, 15.42) * mm, "radius": 0.25 * mm});
            skCircle(sketch, "E381", {"center": v(-2.66, 15.42) * mm, "radius": 0.25 * mm});
            skCircle(sketch, "E382", {"center": v(-8.81, 24.29) * mm, "radius": 0.25 * mm});
            skCircle(sketch, "E383", {"center": v(-9.6, 24.24) * mm, "radius": 0.25 * mm});
            skCircle(sketch, "E384", {"center": v(-10.44, 24.21) * mm, "radius": 0.25 * mm});
            skCircle(sketch, "E385", {"center": v(-11.25, 24.24) * mm, "radius": 0.25 * mm});
            skCircle(sketch, "E386", {"center": v(-8.03, 24.29) * mm, "radius": 0.25 * mm});
            skCircle(sketch, "E387", {"center": v(-12.01, 24.26) * mm, "radius": 0.25 * mm});
            skCircle(sketch, "E388", {"center": v(-12.77, 24.21) * mm, "radius": 0.25 * mm});
            skCircle(sketch, "E389", {"center": v(-6.46, 24.26) * mm, "radius": 0.25 * mm});
            skCircle(sketch, "E390", {"center": v(-5.67, 24.3) * mm, "radius": 0.25 * mm});
            skCircle(sketch, "E391", {"center": v(-4.83, 24.34) * mm, "radius": 0.25 * mm});
            skCircle(sketch, "E392", {"center": v(-4.02, 24.3) * mm, "radius": 0.25 * mm});
            skCircle(sketch, "E393", {"center": v(-7.25, 24.26) * mm, "radius": 0.25 * mm});
            skCircle(sketch, "E394", {"center": v(-3.26, 24.28) * mm, "radius": 0.25 * mm});
            skCircle(sketch, "E395", {"center": v(-2.38, 24.18) * mm, "radius": 0.25 * mm});
            skCircle(sketch, "E396", {"center": v(-8.89, 23.31) * mm, "radius": 0.25 * mm});
            skCircle(sketch, "E397", {"center": v(-9.67, 23.26) * mm, "radius": 0.25 * mm});
            skCircle(sketch, "E398", {"center": v(-10.51, 23.24) * mm, "radius": 0.25 * mm});
            skCircle(sketch, "E399", {"center": v(-11.33, 23.26) * mm, "radius": 0.25 * mm});
            skCircle(sketch, "E400", {"center": v(-8.1, 23.31) * mm, "radius": 0.25 * mm});
            skCircle(sketch, "E401", {"center": v(-13.74, 23.24) * mm, "radius": 0.25 * mm});
            skCircle(sketch, "E402", {"center": v(-12.09, 23.29) * mm, "radius": 0.25 * mm});
            skCircle(sketch, "E403", {"center": v(-12.85, 23.24) * mm, "radius": 0.25 * mm});
            skCircle(sketch, "E404", {"center": v(-6.54, 23.28) * mm, "radius": 0.25 * mm});
            skCircle(sketch, "E405", {"center": v(-5.75, 23.34) * mm, "radius": 0.25 * mm});
            skCircle(sketch, "E406", {"center": v(-4.9, 23.36) * mm, "radius": 0.25 * mm});
            skCircle(sketch, "E407", {"center": v(-4.1, 23.34) * mm, "radius": 0.25 * mm});
            skCircle(sketch, "E408", {"center": v(-7.32, 23.28) * mm, "radius": 0.25 * mm});
            skCircle(sketch, "E409", {"center": v(-1.9, 23.34) * mm, "radius": 0.25 * mm});
            skCircle(sketch, "E410", {"center": v(-3.33, 23.3) * mm, "radius": 0.25 * mm});
            skCircle(sketch, "E411", {"center": v(-1.3, 23.13) * mm, "radius": 0.25 * mm});
            skCircle(sketch, "E412", {"center": v(-2.57, 23.36) * mm, "radius": 0.25 * mm});
            skCircle(sketch, "E413", {"center": v(-8.89, 22.3) * mm, "radius": 0.25 * mm});
            skCircle(sketch, "E414", {"center": v(-9.67, 22.24) * mm, "radius": 0.25 * mm});
            skCircle(sketch, "E415", {"center": v(-10.51, 22.21) * mm, "radius": 0.25 * mm});
            skCircle(sketch, "E416", {"center": v(-11.33, 22.24) * mm, "radius": 0.25 * mm});
            skCircle(sketch, "E417", {"center": v(-8.1, 22.3) * mm, "radius": 0.25 * mm});
            skCircle(sketch, "E418", {"center": v(-13.74, 22.21) * mm, "radius": 0.25 * mm});
            skCircle(sketch, "E419", {"center": v(-12.09, 22.27) * mm, "radius": 0.25 * mm});
            skCircle(sketch, "E420", {"center": v(-14.36, 22.1) * mm, "radius": 0.25 * mm});
            skCircle(sketch, "E421", {"center": v(-12.85, 22.21) * mm, "radius": 0.25 * mm});
            skCircle(sketch, "E422", {"center": v(-6.54, 22.26) * mm, "radius": 0.25 * mm});
            skCircle(sketch, "E423", {"center": v(-5.75, 22.31) * mm, "radius": 0.25 * mm});
            skCircle(sketch, "E424", {"center": v(-4.9, 22.34) * mm, "radius": 0.25 * mm});
            skCircle(sketch, "E425", {"center": v(-4.1, 22.31) * mm, "radius": 0.25 * mm});
            skCircle(sketch, "E426", {"center": v(-7.32, 22.26) * mm, "radius": 0.25 * mm});
            skCircle(sketch, "E427", {"center": v(-1.9, 22.32) * mm, "radius": 0.25 * mm});
            skCircle(sketch, "E428", {"center": v(-3.33, 22.29) * mm, "radius": 0.25 * mm});
            skCircle(sketch, "E429", {"center": v(-1.13, 22.34) * mm, "radius": 0.25 * mm});
            skCircle(sketch, "E430", {"center": v(-2.57, 22.34) * mm, "radius": 0.25 * mm});
            skCircle(sketch, "E431", {"center": v(-8.89, 21.32) * mm, "radius": 0.25 * mm});
            skCircle(sketch, "E432", {"center": v(-9.67, 21.27) * mm, "radius": 0.25 * mm});
            skCircle(sketch, "E433", {"center": v(-10.51, 21.24) * mm, "radius": 0.25 * mm});
            skCircle(sketch, "E434", {"center": v(-11.33, 21.27) * mm, "radius": 0.25 * mm});
            skCircle(sketch, "E435", {"center": v(-8.1, 21.32) * mm, "radius": 0.25 * mm});
            skCircle(sketch, "E436", {"center": v(-13.74, 21.24) * mm, "radius": 0.25 * mm});
            skCircle(sketch, "E437", {"center": v(-12.09, 21.3) * mm, "radius": 0.25 * mm});
            skCircle(sketch, "E438", {"center": v(-14.55, 21.27) * mm, "radius": 0.25 * mm});
            skCircle(sketch, "E439", {"center": v(-0.48, 21.36) * mm, "radius": 0.25 * mm});
            skCircle(sketch, "E440", {"center": v(-12.85, 21.24) * mm, "radius": 0.25 * mm});
            skCircle(sketch, "E441", {"center": v(-6.54, 21.29) * mm, "radius": 0.25 * mm});
            skCircle(sketch, "E442", {"center": v(-5.75, 21.34) * mm, "radius": 0.25 * mm});
            skCircle(sketch, "E443", {"center": v(-4.9, 21.37) * mm, "radius": 0.25 * mm});
            skCircle(sketch, "E444", {"center": v(-4.1, 21.34) * mm, "radius": 0.25 * mm});
            skCircle(sketch, "E445", {"center": v(-7.32, 21.29) * mm, "radius": 0.25 * mm});
            skCircle(sketch, "E446", {"center": v(-1.9, 21.35) * mm, "radius": 0.25 * mm});
            skCircle(sketch, "E447", {"center": v(-3.33, 21.31) * mm, "radius": 0.25 * mm});
            skCircle(sketch, "E448", {"center": v(-1.13, 21.37) * mm, "radius": 0.25 * mm});
            skCircle(sketch, "E449", {"center": v(-2.57, 21.37) * mm, "radius": 0.25 * mm});
            skCircle(sketch, "E450", {"center": v(-8.93, 20.33) * mm, "radius": 0.25 * mm});
            skCircle(sketch, "E451", {"center": v(-9.72, 20.27) * mm, "radius": 0.25 * mm});
            skCircle(sketch, "E452", {"center": v(-10.56, 20.25) * mm, "radius": 0.25 * mm});
            skCircle(sketch, "E453", {"center": v(-11.37, 20.27) * mm, "radius": 0.25 * mm});
            skCircle(sketch, "E454", {"center": v(-8.14, 20.33) * mm, "radius": 0.25 * mm});
            skCircle(sketch, "E455", {"center": v(-13.78, 20.25) * mm, "radius": 0.25 * mm});
            skCircle(sketch, "E456", {"center": v(-12.13, 20.3) * mm, "radius": 0.25 * mm});
            skCircle(sketch, "E457", {"center": v(-14.6, 20.27) * mm, "radius": 0.25 * mm});
            skCircle(sketch, "E458", {"center": v(-0.52, 20.36) * mm, "radius": 0.25 * mm});
            skCircle(sketch, "E459", {"center": v(-12.9, 20.25) * mm, "radius": 0.25 * mm});
            skCircle(sketch, "E460", {"center": v(-6.58, 20.3) * mm, "radius": 0.25 * mm});
            skCircle(sketch, "E461", {"center": v(-5.79, 20.35) * mm, "radius": 0.25 * mm});
            skCircle(sketch, "E462", {"center": v(-4.95, 20.37) * mm, "radius": 0.25 * mm});
            skCircle(sketch, "E463", {"center": v(-4.14, 20.35) * mm, "radius": 0.25 * mm});
            skCircle(sketch, "E464", {"center": v(-7.36, 20.3) * mm, "radius": 0.25 * mm});
            skCircle(sketch, "E465", {"center": v(-1.93, 20.35) * mm, "radius": 0.25 * mm});
            skCircle(sketch, "E466", {"center": v(-3.38, 20.32) * mm, "radius": 0.25 * mm});
            skCircle(sketch, "E467", {"center": v(-1.18, 20.37) * mm, "radius": 0.25 * mm});
            skCircle(sketch, "E468", {"center": v(-2.62, 20.37) * mm, "radius": 0.25 * mm});
            skCircle(sketch, "E469", {"center": v(-8.93, 25) * mm, "radius": 0.25 * mm});
            skCircle(sketch, "E470", {"center": v(-9.72, 24.95) * mm, "radius": 0.25 * mm});
            skCircle(sketch, "E471", {"center": v(-10.56, 24.93) * mm, "radius": 0.25 * mm});
            skCircle(sketch, "E472", {"center": v(-11.37, 24.95) * mm, "radius": 0.25 * mm});
            skCircle(sketch, "E473", {"center": v(-8.14, 25) * mm, "radius": 0.25 * mm});
            skCircle(sketch, "E474", {"center": v(-6.58, 24.97) * mm, "radius": 0.25 * mm});
            skCircle(sketch, "E475", {"center": v(-5.79, 25.03) * mm, "radius": 0.25 * mm});
            skCircle(sketch, "E476", {"center": v(-4.95, 25.05) * mm, "radius": 0.25 * mm});
            skCircle(sketch, "E477", {"center": v(-4.14, 25.03) * mm, "radius": 0.25 * mm});
            skCircle(sketch, "E478", {"center": v(-7.36, 24.97) * mm, "radius": 0.25 * mm});
            skCircle(sketch, "E479.MirrorC", {"center": v(-8.14, -11.43) * mm, "radius": 0.25 * mm});
            skCircle(sketch, "E480.MirrorC", {"center": v(-9.76, -10.39) * mm, "radius": 0.25 * mm});
            skCircle(sketch, "E481.MirrorC", {"center": v(-1.22, -10.49) * mm, "radius": 0.25 * mm});
            skCircle(sketch, "E482.MirrorC", {"center": v(-3.34, -5.55) * mm, "radius": 0.25 * mm});
            skCircle(sketch, "E483.MirrorC", {"center": v(-7.3, -19.3) * mm, "radius": 0.25 * mm});
            skCircle(sketch, "E484.MirrorC", {"center": v(-4.06, -14.42) * mm, "radius": 0.25 * mm});
            skCircle(sketch, "E485.MirrorC", {"center": v(-6.58, -13.4) * mm, "radius": 0.25 * mm});
            skCircle(sketch, "E486.MirrorC", {"center": v(-12.82, -8.47) * mm, "radius": 0.25 * mm});
            skCircle(sketch, "E487.MirrorC", {"center": v(-14.6, -12.35) * mm, "radius": 0.25 * mm});
            skCircle(sketch, "E488.MirrorC", {"center": v(-11.3, -6.5) * mm, "radius": 0.25 * mm});
            skCircle(sketch, "E489.MirrorC", {"center": v(-12.06, -7.5) * mm, "radius": 0.25 * mm});
            skCircle(sketch, "E490.MirrorC", {"center": v(-8.9, -5.56) * mm, "radius": 0.25 * mm});
            skCircle(sketch, "E491.MirrorC", {"center": v(-10.48, -1.54) * mm, "radius": 0.25 * mm});
            skCircle(sketch, "E492.MirrorC", {"center": v(-2.54, -1.66) * mm, "radius": 0.25 * mm});
            skCircle(sketch, "E493.MirrorC", {"center": v(-1.9, -0.65) * mm, "radius": 0.25 * mm});
            skCircle(sketch, "E494.MirrorC", {"center": v(-4.8, -9.57) * mm, "radius": 0.25 * mm});
            skCircle(sketch, "E495.MirrorC", {"center": v(-0.44, -3.65) * mm, "radius": 0.25 * mm});
            skCircle(sketch, "E496.MirrorC", {"center": v(-13.71, -2.51) * mm, "radius": 0.25 * mm});
            skCircle(sketch, "E497.MirrorC", {"center": v(-4.95, -25.05) * mm, "radius": 0.25 * mm});
            skCircle(sketch, "E498.MirrorC", {"center": v(-3.33, -22.29) * mm, "radius": 0.25 * mm});
            skCircle(sketch, "E499.MirrorC", {"center": v(-4.1, -21.34) * mm, "radius": 0.25 * mm});
            skCircle(sketch, "E500.MirrorC", {"center": v(-6.58, -20.3) * mm, "radius": 0.25 * mm});
            skCircle(sketch, "E501.MirrorC", {"center": v(-1.22, -15.42) * mm, "radius": 0.25 * mm});
            skCircle(sketch, "E502.MirrorC", {"center": v(-8.89, -23.31) * mm, "radius": 0.25 * mm});
            skCircle(sketch, "E503.MirrorC", {"center": v(-2.57, -23.36) * mm, "radius": 0.25 * mm});
            skCircle(sketch, "E504.MirrorC", {"center": v(-6.58, -18.33) * mm, "radius": 0.25 * mm});
            skCircle(sketch, "E505.MirrorC", {"center": v(-14.6, -17.29) * mm, "radius": 0.25 * mm});
            skCircle(sketch, "E506.MirrorC", {"center": v(-8.14, -16.37) * mm, "radius": 0.25 * mm});
            skCircle(sketch, "E507.MirrorC", {"center": v(-9.76, -15.32) * mm, "radius": 0.25 * mm});
            skCircle(sketch, "E508.MirrorC", {"center": v(-11.37, -11.38) * mm, "radius": 0.25 * mm});
            skCircle(sketch, "E509.MirrorC", {"center": v(-8.97, -10.44) * mm, "radius": 0.25 * mm});
            skCircle(sketch, "E510.MirrorC", {"center": v(-3.42, -10.43) * mm, "radius": 0.25 * mm});
            skCircle(sketch, "E511.MirrorC", {"center": v(-4.06, -19.36) * mm, "radius": 0.25 * mm});
            skCircle(sketch, "E512.MirrorC", {"center": v(-4.8, -4.63) * mm, "radius": 0.25 * mm});
            skCircle(sketch, "E513.MirrorC", {"center": v(-5.64, -4.6) * mm, "radius": 0.25 * mm});
            skCircle(sketch, "E514.MirrorC", {"center": v(-6.43, -4.55) * mm, "radius": 0.25 * mm});
            skCircle(sketch, "E515.MirrorC", {"center": v(-12.74, -4.5) * mm, "radius": 0.25 * mm});
            skCircle(sketch, "E516.MirrorC", {"center": v(-0.37, -4.62) * mm, "radius": 0.25 * mm});
            skCircle(sketch, "E517.MirrorC", {"center": v(-14.45, -4.53) * mm, "radius": 0.25 * mm});
            skCircle(sketch, "E518.MirrorC", {"center": v(-11.98, -4.56) * mm, "radius": 0.25 * mm});
            skCircle(sketch, "E519.MirrorC", {"center": v(-13.64, -4.5) * mm, "radius": 0.25 * mm});
            skCircle(sketch, "E520.MirrorC", {"center": v(-8, -4.59) * mm, "radius": 0.25 * mm});
            skCircle(sketch, "E521.MirrorC", {"center": v(-11.22, -4.53) * mm, "radius": 0.25 * mm});
            skCircle(sketch, "E522.MirrorC", {"center": v(-10.4, -4.5) * mm, "radius": 0.25 * mm});
            skCircle(sketch, "E523.MirrorC", {"center": v(-9.57, -4.53) * mm, "radius": 0.25 * mm});
            skCircle(sketch, "E524.MirrorC", {"center": v(-1.9, -5.59) * mm, "radius": 0.25 * mm});
            skCircle(sketch, "E525.MirrorC", {"center": v(-8.78, -4.59) * mm, "radius": 0.25 * mm});
            skCircle(sketch, "E526.MirrorC", {"center": v(-4.88, -14.45) * mm, "radius": 0.25 * mm});
            skCircle(sketch, "E527.MirrorC", {"center": v(-12.9, -13.35) * mm, "radius": 0.25 * mm});
            skCircle(sketch, "E528.MirrorC", {"center": v(-12.13, -12.38) * mm, "radius": 0.25 * mm});
            skCircle(sketch, "E529.MirrorC", {"center": v(-0.44, -8.59) * mm, "radius": 0.25 * mm});
            skCircle(sketch, "E530.MirrorC", {"center": v(-13.71, -7.45) * mm, "radius": 0.25 * mm});
            skCircle(sketch, "E531.MirrorC", {"center": v(-10.48, -6.47) * mm, "radius": 0.25 * mm});
            skCircle(sketch, "E532.MirrorC", {"center": v(-1.78, -4.61) * mm, "radius": 0.25 * mm});
            skCircle(sketch, "E533.MirrorC", {"center": v(-9.64, -1.56) * mm, "radius": 0.25 * mm});
            skCircle(sketch, "E534.MirrorC", {"center": v(-2.54, -6.6) * mm, "radius": 0.25 * mm});
            skCircle(sketch, "E535.MirrorC", {"center": v(-1.1, -1.66) * mm, "radius": 0.25 * mm});
            skCircle(sketch, "E536.MirrorC", {"center": v(-7.33, -0.6) * mm, "radius": 0.25 * mm});
            skCircle(sketch, "E537.MirrorC", {"center": v(-5.64, -9.54) * mm, "radius": 0.25 * mm});
            skCircle(sketch, "E538.MirrorC", {"center": v(-7.22, -4.55) * mm, "radius": 0.25 * mm});
            skCircle(sketch, "E539.MirrorC", {"center": v(-14.52, -3.56) * mm, "radius": 0.25 * mm});
            skCircle(sketch, "E540.MirrorC", {"center": v(-8.07, -2.59) * mm, "radius": 0.25 * mm});
            skCircle(sketch, "E541.MirrorC", {"center": v(-3.99, -4.6) * mm, "radius": 0.25 * mm});
            skCircle(sketch, "E542.MirrorC", {"center": v(-1.9, -22.32) * mm, "radius": 0.25 * mm});
            skCircle(sketch, "E543.MirrorC", {"center": v(-5.79, -25.03) * mm, "radius": 0.25 * mm});
            skCircle(sketch, "E544.MirrorC", {"center": v(-4.9, -21.37) * mm, "radius": 0.25 * mm});
            skCircle(sketch, "E545.MirrorC", {"center": v(-12.9, -20.25) * mm, "radius": 0.25 * mm});
            skCircle(sketch, "E546.MirrorC", {"center": v(-1.3, -23.13) * mm, "radius": 0.25 * mm});
            skCircle(sketch, "E547.MirrorC", {"center": v(-2.38, -24.18) * mm, "radius": 0.25 * mm});
            skCircle(sketch, "E548.MirrorC", {"center": v(-3.42, -15.37) * mm, "radius": 0.25 * mm});
            skCircle(sketch, "E549.MirrorC", {"center": v(-12.13, -17.32) * mm, "radius": 0.25 * mm});
            skCircle(sketch, "E550.MirrorC", {"center": v(-12.9, -18.29) * mm, "radius": 0.25 * mm});
            skCircle(sketch, "E551.MirrorC", {"center": v(-11.37, -16.32) * mm, "radius": 0.25 * mm});
            skCircle(sketch, "E552.MirrorC", {"center": v(-8.97, -15.38) * mm, "radius": 0.25 * mm});
            skCircle(sketch, "E553.MirrorC", {"center": v(-2.62, -11.48) * mm, "radius": 0.25 * mm});
            skCircle(sketch, "E554.MirrorC", {"center": v(-10.56, -11.35) * mm, "radius": 0.25 * mm});
            skCircle(sketch, "E555.MirrorC", {"center": v(-1.98, -10.47) * mm, "radius": 0.25 * mm});
            skCircle(sketch, "E556.MirrorC", {"center": v(-4.88, -19.39) * mm, "radius": 0.25 * mm});
            skCircle(sketch, "E557.MirrorC", {"center": v(-7.33, -5.53) * mm, "radius": 0.25 * mm});
            skCircle(sketch, "E558.MirrorC", {"center": v(-5.72, -14.42) * mm, "radius": 0.25 * mm});
            skCircle(sketch, "E559.MirrorC", {"center": v(-0.52, -13.46) * mm, "radius": 0.25 * mm});
            skCircle(sketch, "E560.MirrorC", {"center": v(-13.79, -12.33) * mm, "radius": 0.25 * mm});
            skCircle(sketch, "E561.MirrorC", {"center": v(-14.52, -8.5) * mm, "radius": 0.25 * mm});
            skCircle(sketch, "E562.MirrorC", {"center": v(-8.07, -7.53) * mm, "radius": 0.25 * mm});
            skCircle(sketch, "E563.MirrorC", {"center": v(-1.1, -6.6) * mm, "radius": 0.25 * mm});
            skCircle(sketch, "E564.MirrorC", {"center": v(-9.64, -6.5) * mm, "radius": 0.25 * mm});
            skCircle(sketch, "E565.MirrorC", {"center": v(-8.86, -1.62) * mm, "radius": 0.25 * mm});
            skCircle(sketch, "E566.MirrorC", {"center": v(-3.3, -1.61) * mm, "radius": 0.25 * mm});
            skCircle(sketch, "E567.MirrorC", {"center": v(-4.1, -0.64) * mm, "radius": 0.25 * mm});
            skCircle(sketch, "E568.MirrorC", {"center": v(-6.43, -9.5) * mm, "radius": 0.25 * mm});
            skCircle(sketch, "E569.MirrorC", {"center": v(-12.06, -3.59) * mm, "radius": 0.25 * mm});
            skCircle(sketch, "E570.MirrorC", {"center": v(-11.3, -2.54) * mm, "radius": 0.25 * mm});
            skCircle(sketch, "E571.MirrorC", {"center": v(-6.58, -24.97) * mm, "radius": 0.25 * mm});
            skCircle(sketch, "E572.MirrorC", {"center": v(-7.32, -22.26) * mm, "radius": 0.25 * mm});
            skCircle(sketch, "E573.MirrorC", {"center": v(-5.75, -21.34) * mm, "radius": 0.25 * mm});
            skCircle(sketch, "E574.MirrorC", {"center": v(-1.98, -15.4) * mm, "radius": 0.25 * mm});
            skCircle(sketch, "E575.MirrorC", {"center": v(-0.52, -20.36) * mm, "radius": 0.25 * mm});
            skCircle(sketch, "E576.MirrorC", {"center": v(-3.33, -23.3) * mm, "radius": 0.25 * mm});
            skCircle(sketch, "E577.MirrorC", {"center": v(-3.26, -24.28) * mm, "radius": 0.25 * mm});
            skCircle(sketch, "E578.MirrorC", {"center": v(-0.52, -18.4) * mm, "radius": 0.25 * mm});
            skCircle(sketch, "E579.MirrorC", {"center": v(-13.79, -17.26) * mm, "radius": 0.25 * mm});
            skCircle(sketch, "E580.MirrorC", {"center": v(-10.56, -16.3) * mm, "radius": 0.25 * mm});
            skCircle(sketch, "E581.MirrorC", {"center": v(-2.62, -16.42) * mm, "radius": 0.25 * mm});
            skCircle(sketch, "E582.MirrorC", {"center": v(-1.18, -11.48) * mm, "radius": 0.25 * mm});
            skCircle(sketch, "E583.MirrorC", {"center": v(-9.72, -11.38) * mm, "radius": 0.25 * mm});
            skCircle(sketch, "E584.MirrorC", {"center": v(-5.72, -19.36) * mm, "radius": 0.25 * mm});
            skCircle(sketch, "E585.MirrorC", {"center": v(-7.4, -10.4) * mm, "radius": 0.25 * mm});
            skCircle(sketch, "E586.MirrorC", {"center": v(-4.1, -5.58) * mm, "radius": 0.25 * mm});
            skCircle(sketch, "E587.MirrorC", {"center": v(-6.5, -14.37) * mm, "radius": 0.25 * mm});
            skCircle(sketch, "E588.MirrorC", {"center": v(-14.6, -13.38) * mm, "radius": 0.25 * mm});
            skCircle(sketch, "E589.MirrorC", {"center": v(-8.14, -12.4) * mm, "radius": 0.25 * mm});
            skCircle(sketch, "E590.MirrorC", {"center": v(-12.06, -8.52) * mm, "radius": 0.25 * mm});
            skCircle(sketch, "E591.MirrorC", {"center": v(-11.3, -7.47) * mm, "radius": 0.25 * mm});
            skCircle(sketch, "E592.MirrorC", {"center": v(-8.86, -6.55) * mm, "radius": 0.25 * mm});
            skCircle(sketch, "E593.MirrorC", {"center": v(-3.3, -6.55) * mm, "radius": 0.25 * mm});
            skCircle(sketch, "E594.MirrorC", {"center": v(-2.54, -2.64) * mm, "radius": 0.25 * mm});
            skCircle(sketch, "E595.MirrorC", {"center": v(-1.86, -1.64) * mm, "radius": 0.25 * mm});
            skCircle(sketch, "E596.MirrorC", {"center": v(-12.74, -9.44) * mm, "radius": 0.25 * mm});
            skCircle(sketch, "E597.MirrorC", {"center": v(-4.92, -0.67) * mm, "radius": 0.25 * mm});
            skCircle(sketch, "E598.MirrorC", {"center": v(-13.71, -3.53) * mm, "radius": 0.25 * mm});
            skCircle(sketch, "E599.MirrorC", {"center": v(-10.48, -2.51) * mm, "radius": 0.25 * mm});
            skCircle(sketch, "E600.MirrorC", {"center": v(-4.1, -22.31) * mm, "radius": 0.25 * mm});
            skCircle(sketch, "E601.MirrorC", {"center": v(-6.54, -21.29) * mm, "radius": 0.25 * mm});
            skCircle(sketch, "E602.MirrorC", {"center": v(-7.4, -15.34) * mm, "radius": 0.25 * mm});
            skCircle(sketch, "E603.MirrorC", {"center": v(-14.6, -20.27) * mm, "radius": 0.25 * mm});
            skCircle(sketch, "E604.MirrorC", {"center": v(-7.25, -24.26) * mm, "radius": 0.25 * mm});
            skCircle(sketch, "E605.MirrorC", {"center": v(-1.9, -23.34) * mm, "radius": 0.25 * mm});
            skCircle(sketch, "E606.MirrorC", {"center": v(-14.6, -18.31) * mm, "radius": 0.25 * mm});
            skCircle(sketch, "E607.MirrorC", {"center": v(-8.14, -17.34) * mm, "radius": 0.25 * mm});
            skCircle(sketch, "E608.MirrorC", {"center": v(-9.72, -16.32) * mm, "radius": 0.25 * mm});
            skCircle(sketch, "E609.MirrorC", {"center": v(-1.18, -16.42) * mm, "radius": 0.25 * mm});
            skCircle(sketch, "E610.MirrorC", {"center": v(-8.93, -11.43) * mm, "radius": 0.25 * mm});
            skCircle(sketch, "E611.MirrorC", {"center": v(-3.38, -11.43) * mm, "radius": 0.25 * mm});
            skCircle(sketch, "E612.MirrorC", {"center": v(-4.18, -10.46) * mm, "radius": 0.25 * mm});
            skCircle(sketch, "E613.MirrorC", {"center": v(-6.5, -19.3) * mm, "radius": 0.25 * mm});
            skCircle(sketch, "E614.MirrorC", {"center": v(-4.92, -5.6) * mm, "radius": 0.25 * mm});
            skCircle(sketch, "E615.MirrorC", {"center": v(-12.82, -14.32) * mm, "radius": 0.25 * mm});
            skCircle(sketch, "E616.MirrorC", {"center": v(-12.13, -13.4) * mm, "radius": 0.25 * mm});
            skCircle(sketch, "E617.MirrorC", {"center": v(-11.37, -12.35) * mm, "radius": 0.25 * mm});
            skCircle(sketch, "E618.MirrorC", {"center": v(-13.71, -8.47) * mm, "radius": 0.25 * mm});
            skCircle(sketch, "E619.MirrorC", {"center": v(-2.54, -7.57) * mm, "radius": 0.25 * mm});
            skCircle(sketch, "E620.MirrorC", {"center": v(-10.48, -7.45) * mm, "radius": 0.25 * mm});
            skCircle(sketch, "E621.MirrorC", {"center": v(-1.86, -6.58) * mm, "radius": 0.25 * mm});
            skCircle(sketch, "E622.MirrorC", {"center": v(-1.1, -2.64) * mm, "radius": 0.25 * mm});
            skCircle(sketch, "E623.MirrorC", {"center": v(-7.3, -1.58) * mm, "radius": 0.25 * mm});
            skCircle(sketch, "E624.MirrorC", {"center": v(-5.76, -0.64) * mm, "radius": 0.25 * mm});
            skCircle(sketch, "E625.MirrorC", {"center": v(-0.37, -9.56) * mm, "radius": 0.25 * mm});
            skCircle(sketch, "E626.MirrorC", {"center": v(-8.14, -25) * mm, "radius": 0.25 * mm});
            skCircle(sketch, "E627.MirrorC", {"center": v(-4.9, -22.34) * mm, "radius": 0.25 * mm});
            skCircle(sketch, "E628.MirrorC", {"center": v(-7.32, -23.28) * mm, "radius": 0.25 * mm});
            skCircle(sketch, "E629.MirrorC", {"center": v(-13.79, -18.29) * mm, "radius": 0.25 * mm});
            skCircle(sketch, "E630.MirrorC", {"center": v(-5.83, -10.46) * mm, "radius": 0.25 * mm});
            skCircle(sketch, "E631.MirrorC", {"center": v(-0.44, -19.38) * mm, "radius": 0.25 * mm});
            skCircle(sketch, "E632.MirrorC", {"center": v(-8.14, -13.43) * mm, "radius": 0.25 * mm});
            skCircle(sketch, "E633.MirrorC", {"center": v(-9.72, -12.35) * mm, "radius": 0.25 * mm});
            skCircle(sketch, "E634.MirrorC", {"center": v(-10.56, -17.26) * mm, "radius": 0.25 * mm});
            skCircle(sketch, "E635.MirrorC", {"center": v(-1.18, -12.45) * mm, "radius": 0.25 * mm});
            skCircle(sketch, "E636.MirrorC", {"center": v(-7.37, -11.4) * mm, "radius": 0.25 * mm});
            skCircle(sketch, "E637.MirrorC", {"center": v(-3.3, -7.52) * mm, "radius": 0.25 * mm});
            skCircle(sketch, "E638.MirrorC", {"center": v(-14.52, -14.35) * mm, "radius": 0.25 * mm});
            skCircle(sketch, "E639.MirrorC", {"center": v(-6.55, -5.53) * mm, "radius": 0.25 * mm});
            skCircle(sketch, "E640.MirrorC", {"center": v(-4.06, -6.57) * mm, "radius": 0.25 * mm});
            skCircle(sketch, "E641.MirrorC", {"center": v(-11.98, -9.5) * mm, "radius": 0.25 * mm});
            skCircle(sketch, "E642.MirrorC", {"center": v(-12.86, -0.54) * mm, "radius": 0.25 * mm});
            skCircle(sketch, "E643.MirrorC", {"center": v(-11.3, -8.5) * mm, "radius": 0.25 * mm});
            skCircle(sketch, "E644.MirrorC", {"center": v(-8.86, -7.53) * mm, "radius": 0.25 * mm});
            skCircle(sketch, "E645.MirrorC", {"center": v(-10.48, -3.53) * mm, "radius": 0.25 * mm});
            skCircle(sketch, "E646.MirrorC", {"center": v(-2.54, -3.66) * mm, "radius": 0.25 * mm});
            skCircle(sketch, "E647.MirrorC", {"center": v(-1.86, -2.62) * mm, "radius": 0.25 * mm});
            skCircle(sketch, "E648.MirrorC", {"center": v(-4.88, -1.66) * mm, "radius": 0.25 * mm});
            skCircle(sketch, "E649.MirrorC", {"center": v(-2.66, -15.42) * mm, "radius": 0.25 * mm});
            skCircle(sketch, "E650.MirrorC", {"center": v(-10.56, -24.93) * mm, "radius": 0.25 * mm});
            skCircle(sketch, "E651.MirrorC", {"center": v(-13.78, -20.25) * mm, "radius": 0.25 * mm});
            skCircle(sketch, "E652.MirrorC", {"center": v(-4.1, -23.34) * mm, "radius": 0.25 * mm});
            skCircle(sketch, "E653.MirrorC", {"center": v(-0.48, -21.36) * mm, "radius": 0.25 * mm});
            skCircle(sketch, "E654.MirrorC", {"center": v(-5.75, -22.31) * mm, "radius": 0.25 * mm});
            skCircle(sketch, "E655.MirrorC", {"center": v(-2.62, -17.39) * mm, "radius": 0.25 * mm});
            skCircle(sketch, "E656.MirrorC", {"center": v(-1.93, -16.4) * mm, "radius": 0.25 * mm});
            skCircle(sketch, "E657.MirrorC", {"center": v(-4.83, -24.34) * mm, "radius": 0.25 * mm});
            skCircle(sketch, "E658.MirrorC", {"center": v(-5, -15.42) * mm, "radius": 0.25 * mm});
            skCircle(sketch, "E659.MirrorC", {"center": v(-7.36, -24.97) * mm, "radius": 0.25 * mm});
            skCircle(sketch, "E660.MirrorC", {"center": v(-8.93, -12.4) * mm, "radius": 0.25 * mm});
            skCircle(sketch, "E661.MirrorC", {"center": v(-11.37, -13.38) * mm, "radius": 0.25 * mm});
            skCircle(sketch, "E662.MirrorC", {"center": v(-4.14, -11.45) * mm, "radius": 0.25 * mm});
            skCircle(sketch, "E663.MirrorC", {"center": v(-3.38, -12.4) * mm, "radius": 0.25 * mm});
            skCircle(sketch, "E664.MirrorC", {"center": v(-12.06, -14.38) * mm, "radius": 0.25 * mm});
            skCircle(sketch, "E665.MirrorC", {"center": v(-1.86, -7.55) * mm, "radius": 0.25 * mm});
            skCircle(sketch, "E666.MirrorC", {"center": v(-4.88, -6.6) * mm, "radius": 0.25 * mm});
            skCircle(sketch, "E667.MirrorC", {"center": v(-13.64, -9.44) * mm, "radius": 0.25 * mm});
            skCircle(sketch, "E668.MirrorC", {"center": v(-12.86, -5.48) * mm, "radius": 0.25 * mm});
            skCircle(sketch, "E669.MirrorC", {"center": v(-0.49, -0.66) * mm, "radius": 0.25 * mm});
            skCircle(sketch, "E670.MirrorC", {"center": v(-10.48, -8.47) * mm, "radius": 0.25 * mm});
            skCircle(sketch, "E671.MirrorC", {"center": v(-2.54, -8.6) * mm, "radius": 0.25 * mm});
            skCircle(sketch, "E672.MirrorC", {"center": v(-9.64, -3.56) * mm, "radius": 0.25 * mm});
            skCircle(sketch, "E673.MirrorC", {"center": v(-2.57, -22.34) * mm, "radius": 0.25 * mm});
            skCircle(sketch, "E674.MirrorC", {"center": v(-1.1, -3.66) * mm, "radius": 0.25 * mm});
            skCircle(sketch, "E675.MirrorC", {"center": v(-4.95, -20.37) * mm, "radius": 0.25 * mm});
            skCircle(sketch, "E676.MirrorC", {"center": v(-8.81, -24.29) * mm, "radius": 0.25 * mm});
            skCircle(sketch, "E677.MirrorC", {"center": v(-10.51, -23.24) * mm, "radius": 0.25 * mm});
            skCircle(sketch, "E678.MirrorC", {"center": v(-9.67, -22.24) * mm, "radius": 0.25 * mm});
            skCircle(sketch, "E679.MirrorC", {"center": v(-7.3, -2.56) * mm, "radius": 0.25 * mm});
            skCircle(sketch, "E680.MirrorC", {"center": v(-5.72, -1.64) * mm, "radius": 0.25 * mm});
            skCircle(sketch, "E681.MirrorC", {"center": v(-4.14, -25.03) * mm, "radius": 0.25 * mm});
            skCircle(sketch, "E682.MirrorC", {"center": v(-14.55, -21.27) * mm, "radius": 0.25 * mm});
            skCircle(sketch, "E683.MirrorC", {"center": v(-8.14, -20.33) * mm, "radius": 0.25 * mm});
            skCircle(sketch, "E684.MirrorC", {"center": v(-6.54, -22.26) * mm, "radius": 0.25 * mm});
            skCircle(sketch, "E685.MirrorC", {"center": v(-9.72, -24.95) * mm, "radius": 0.25 * mm});
            skCircle(sketch, "E686.MirrorC", {"center": v(-1.18, -17.39) * mm, "radius": 0.25 * mm});
            skCircle(sketch, "E687.MirrorC", {"center": v(-4.9, -23.36) * mm, "radius": 0.25 * mm});
            skCircle(sketch, "E688.MirrorC", {"center": v(-5.83, -15.4) * mm, "radius": 0.25 * mm});
            skCircle(sketch, "E689.MirrorC", {"center": v(-7.37, -16.34) * mm, "radius": 0.25 * mm});
            skCircle(sketch, "E690.MirrorC", {"center": v(-6.62, -10.4) * mm, "radius": 0.25 * mm});
            skCircle(sketch, "E691.MirrorC", {"center": v(-5.67, -24.3) * mm, "radius": 0.25 * mm});
            skCircle(sketch, "E692.MirrorC", {"center": v(-14.52, -19.29) * mm, "radius": 0.25 * mm});
            skCircle(sketch, "E693.MirrorC", {"center": v(-9.72, -17.29) * mm, "radius": 0.25 * mm});
            skCircle(sketch, "E694.MirrorC", {"center": v(-8.14, -18.36) * mm, "radius": 0.25 * mm});
            skCircle(sketch, "E695.MirrorC", {"center": v(-8.93, -16.37) * mm, "radius": 0.25 * mm});
            skCircle(sketch, "E696.MirrorC", {"center": v(-3.38, -16.36) * mm, "radius": 0.25 * mm});
            skCircle(sketch, "E697.MirrorC", {"center": v(-4.18, -15.4) * mm, "radius": 0.25 * mm});
            skCircle(sketch, "E698.MirrorC", {"center": v(-7.3, -7.5) * mm, "radius": 0.25 * mm});
            skCircle(sketch, "E699.MirrorC", {"center": v(-5.72, -6.57) * mm, "radius": 0.25 * mm});
            skCircle(sketch, "E700.MirrorC", {"center": v(-13.71, -14.32) * mm, "radius": 0.25 * mm});
            skCircle(sketch, "E701.MirrorC", {"center": v(-0.49, -5.6) * mm, "radius": 0.25 * mm});
            skCircle(sketch, "E702.MirrorC", {"center": v(-8, -9.52) * mm, "radius": 0.25 * mm});
            skCircle(sketch, "E703.MirrorC", {"center": v(-14.57, -0.57) * mm, "radius": 0.25 * mm});
            skCircle(sketch, "E704.MirrorC", {"center": v(-9.64, -8.5) * mm, "radius": 0.25 * mm});
            skCircle(sketch, "E705.MirrorC", {"center": v(-1.1, -8.6) * mm, "radius": 0.25 * mm});
            skCircle(sketch, "E706.MirrorC", {"center": v(-3.3, -3.6) * mm, "radius": 0.25 * mm});
            skCircle(sketch, "E707.MirrorC", {"center": v(-8.86, -3.61) * mm, "radius": 0.25 * mm});
            skCircle(sketch, "E708.MirrorC", {"center": v(-4.06, -2.6) * mm, "radius": 0.25 * mm});
            skCircle(sketch, "E709.MirrorC", {"center": v(-6.5, -1.58) * mm, "radius": 0.25 * mm});
            skCircle(sketch, "E710.MirrorC", {"center": v(-5, -10.49) * mm, "radius": 0.25 * mm});
            skCircle(sketch, "E711.MirrorC", {"center": v(-1.9, -21.35) * mm, "radius": 0.25 * mm});
            skCircle(sketch, "E712.MirrorC", {"center": v(-4.02, -24.3) * mm, "radius": 0.25 * mm});
            skCircle(sketch, "E713.MirrorC", {"center": v(-12.09, -21.3) * mm, "radius": 0.25 * mm});
            skCircle(sketch, "E714.MirrorC", {"center": v(-8.93, -25) * mm, "radius": 0.25 * mm});
            skCircle(sketch, "E715.MirrorC", {"center": v(-12.85, -22.21) * mm, "radius": 0.25 * mm});
            skCircle(sketch, "E716.MirrorC", {"center": v(-11.37, -20.27) * mm, "radius": 0.25 * mm});
            skCircle(sketch, "E717.MirrorC", {"center": v(-5.75, -23.34) * mm, "radius": 0.25 * mm});
            skCircle(sketch, "E718.MirrorC", {"center": v(-3.38, -17.34) * mm, "radius": 0.25 * mm});
            skCircle(sketch, "E719.MirrorC", {"center": v(-6.62, -15.34) * mm, "radius": 0.25 * mm});
            skCircle(sketch, "E720.MirrorC", {"center": v(-4.14, -16.4) * mm, "radius": 0.25 * mm});
            skCircle(sketch, "E721.MirrorC", {"center": v(-12.94, -10.36) * mm, "radius": 0.25 * mm});
            skCircle(sketch, "E722.MirrorC", {"center": v(-6.46, -24.26) * mm, "radius": 0.25 * mm});
            skCircle(sketch, "E723.MirrorC", {"center": v(-11.37, -18.31) * mm, "radius": 0.25 * mm});
            skCircle(sketch, "E724.MirrorC", {"center": v(-12.06, -19.31) * mm, "radius": 0.25 * mm});
            skCircle(sketch, "E725.MirrorC", {"center": v(-8.93, -17.34) * mm, "radius": 0.25 * mm});
            skCircle(sketch, "E726.MirrorC", {"center": v(-10.56, -13.35) * mm, "radius": 0.25 * mm});
            skCircle(sketch, "E727.MirrorC", {"center": v(-2.62, -13.47) * mm, "radius": 0.25 * mm});
            skCircle(sketch, "E728.MirrorC", {"center": v(-1.93, -12.43) * mm, "radius": 0.25 * mm});
            skCircle(sketch, "E729.MirrorC", {"center": v(-4.95, -11.48) * mm, "radius": 0.25 * mm});
            skCircle(sketch, "E730.MirrorC", {"center": v(-12.1, -0.6) * mm, "radius": 0.25 * mm});
            skCircle(sketch, "E731.MirrorC", {"center": v(-11.22, -9.47) * mm, "radius": 0.25 * mm});
            skCircle(sketch, "E732.MirrorC", {"center": v(-8.86, -8.55) * mm, "radius": 0.25 * mm});
            skCircle(sketch, "E733.MirrorC", {"center": v(-3.3, -8.54) * mm, "radius": 0.25 * mm});
            skCircle(sketch, "E734.MirrorC", {"center": v(-2.47, -4.63) * mm, "radius": 0.25 * mm});
            skCircle(sketch, "E735.MirrorC", {"center": v(-1.86, -3.64) * mm, "radius": 0.25 * mm});
            skCircle(sketch, "E736.MirrorC", {"center": v(-4.88, -2.64) * mm, "radius": 0.25 * mm});
            skCircle(sketch, "E737.MirrorC", {"center": v(-12.82, -1.54) * mm, "radius": 0.25 * mm});
            skCircle(sketch, "E738.MirrorC", {"center": v(-12.82, -19.26) * mm, "radius": 0.25 * mm});
            skCircle(sketch, "E739.MirrorC", {"center": v(-11.37, -17.29) * mm, "radius": 0.25 * mm});
            skCircle(sketch, "E740.MirrorC", {"center": v(-13.74, -21.24) * mm, "radius": 0.25 * mm});
            skCircle(sketch, "E741.MirrorC", {"center": v(-2.62, -20.37) * mm, "radius": 0.25 * mm});
            skCircle(sketch, "E742.MirrorC", {"center": v(-10.56, -20.25) * mm, "radius": 0.25 * mm});
            skCircle(sketch, "E743.MirrorC", {"center": v(-14.36, -22.1) * mm, "radius": 0.25 * mm});
            skCircle(sketch, "E744.MirrorC", {"center": v(-4.95, -18.41) * mm, "radius": 0.25 * mm});
            skCircle(sketch, "E745.MirrorC", {"center": v(-6.54, -23.28) * mm, "radius": 0.25 * mm});
            skCircle(sketch, "E746.MirrorC", {"center": v(-1.93, -17.37) * mm, "radius": 0.25 * mm});
            skCircle(sketch, "E747.MirrorC", {"center": v(-4.95, -16.42) * mm, "radius": 0.25 * mm});
            skCircle(sketch, "E748.MirrorC", {"center": v(-12.94, -15.3) * mm, "radius": 0.25 * mm});
            skCircle(sketch, "E749.MirrorC", {"center": v(-12.77, -24.21) * mm, "radius": 0.25 * mm});
            skCircle(sketch, "E750.MirrorC", {"center": v(-9.67, -23.26) * mm, "radius": 0.25 * mm});
            skCircle(sketch, "E751.MirrorC", {"center": v(-0.56, -10.48) * mm, "radius": 0.25 * mm});
            skCircle(sketch, "E752.MirrorC", {"center": v(-13.71, -19.26) * mm, "radius": 0.25 * mm});
            skCircle(sketch, "E753.MirrorC", {"center": v(-12.9, -17.26) * mm, "radius": 0.25 * mm});
            skCircle(sketch, "E754.MirrorC", {"center": v(-10.56, -18.29) * mm, "radius": 0.25 * mm});
            skCircle(sketch, "E755.MirrorC", {"center": v(-1.18, -13.47) * mm, "radius": 0.25 * mm});
            skCircle(sketch, "E756.MirrorC", {"center": v(-9.72, -13.38) * mm, "radius": 0.25 * mm});
            skCircle(sketch, "E757.MirrorC", {"center": v(-2.62, -18.41) * mm, "radius": 0.25 * mm});
            skCircle(sketch, "E758.MirrorC", {"center": v(-7.37, -12.37) * mm, "radius": 0.25 * mm});
            skCircle(sketch, "E759.MirrorC", {"center": v(-5.8, -11.45) * mm, "radius": 0.25 * mm});
            skCircle(sketch, "E760.MirrorC", {"center": v(-4.06, -7.55) * mm, "radius": 0.25 * mm});
            skCircle(sketch, "E761.MirrorC", {"center": v(-6.5, -6.52) * mm, "radius": 0.25 * mm});
            skCircle(sketch, "E762.MirrorC", {"center": v(-14.57, -5.5) * mm, "radius": 0.25 * mm});
            skCircle(sketch, "E763.MirrorC", {"center": v(-8.07, -14.4) * mm, "radius": 0.25 * mm});
            skCircle(sketch, "E764.MirrorC", {"center": v(-1.03, -4.63) * mm, "radius": 0.25 * mm});
            skCircle(sketch, "E765.MirrorC", {"center": v(-7.3, -3.58) * mm, "radius": 0.25 * mm});
            skCircle(sketch, "E766.MirrorC", {"center": v(-5.72, -2.6) * mm, "radius": 0.25 * mm});
            skCircle(sketch, "E767.MirrorC", {"center": v(-0.44, -1.65) * mm, "radius": 0.25 * mm});
            skCircle(sketch, "E768.MirrorC", {"center": v(-12.13, -16.34) * mm, "radius": 0.25 * mm});
            skCircle(sketch, "E769.MirrorC", {"center": v(-13.79, -11.35) * mm, "radius": 0.25 * mm});
            skCircle(sketch, "E770.MirrorC", {"center": v(-11.41, -15.32) * mm, "radius": 0.25 * mm});
            skCircle(sketch, "E771.MirrorC", {"center": v(-10.6, -10.36) * mm, "radius": 0.25 * mm});
            skCircle(sketch, "E772.MirrorC", {"center": v(-1.86, -19.37) * mm, "radius": 0.25 * mm});
            skCircle(sketch, "E773.MirrorC", {"center": v(-2.66, -10.49) * mm, "radius": 0.25 * mm});
            skCircle(sketch, "E774.MirrorC", {"center": v(-1.14, -5.6) * mm, "radius": 0.25 * mm});
            skCircle(sketch, "E775.MirrorC", {"center": v(-8.1, -21.32) * mm, "radius": 0.25 * mm});
            skCircle(sketch, "E776.MirrorC", {"center": v(-9.72, -20.27) * mm, "radius": 0.25 * mm});
            skCircle(sketch, "E777.MirrorC", {"center": v(-1.18, -20.37) * mm, "radius": 0.25 * mm});
            skCircle(sketch, "E778.MirrorC", {"center": v(-12.85, -23.24) * mm, "radius": 0.25 * mm});
            skCircle(sketch, "E779.MirrorC", {"center": v(-12.09, -22.27) * mm, "radius": 0.25 * mm});
            skCircle(sketch, "E780.MirrorC", {"center": v(-7.37, -17.31) * mm, "radius": 0.25 * mm});
            skCircle(sketch, "E781.MirrorC", {"center": v(-5.8, -16.4) * mm, "radius": 0.25 * mm});
            skCircle(sketch, "E782.MirrorC", {"center": v(-12.13, -18.34) * mm, "radius": 0.25 * mm});
            skCircle(sketch, "E783.MirrorC", {"center": v(-0.56, -15.41) * mm, "radius": 0.25 * mm});
            skCircle(sketch, "E784.MirrorC", {"center": v(-12.01, -24.26) * mm, "radius": 0.25 * mm});
            skCircle(sketch, "E785.MirrorC", {"center": v(-14.64, -10.39) * mm, "radius": 0.25 * mm});
            skCircle(sketch, "E786.MirrorC", {"center": v(-8.07, -19.34) * mm, "radius": 0.25 * mm});
            skCircle(sketch, "E787.MirrorC", {"center": v(-7.3, -14.37) * mm, "radius": 0.25 * mm});
            skCircle(sketch, "E788.MirrorC", {"center": v(-0.52, -12.44) * mm, "radius": 0.25 * mm});
            skCircle(sketch, "E789.MirrorC", {"center": v(-13.79, -13.35) * mm, "radius": 0.25 * mm});
            skCircle(sketch, "E790.MirrorC", {"center": v(-9.72, -18.31) * mm, "radius": 0.25 * mm});
            skCircle(sketch, "E791.MirrorC", {"center": v(-1.18, -18.41) * mm, "radius": 0.25 * mm});
            skCircle(sketch, "E792.MirrorC", {"center": v(-8.93, -13.43) * mm, "radius": 0.25 * mm});
            skCircle(sketch, "E793.MirrorC", {"center": v(-3.38, -13.42) * mm, "radius": 0.25 * mm});
            skCircle(sketch, "E794.MirrorC", {"center": v(-5.8, -13.45) * mm, "radius": 0.25 * mm});
            skCircle(sketch, "E795.MirrorC", {"center": v(-4.14, -12.43) * mm, "radius": 0.25 * mm});
            skCircle(sketch, "E796.MirrorC", {"center": v(-6.58, -11.4) * mm, "radius": 0.25 * mm});
            skCircle(sketch, "E797.MirrorC", {"center": v(-12.82, -6.47) * mm, "radius": 0.25 * mm});
            skCircle(sketch, "E798.MirrorC", {"center": v(-4.88, -7.57) * mm, "radius": 0.25 * mm});
            skCircle(sketch, "E799.MirrorC", {"center": v(-12.1, -5.53) * mm, "radius": 0.25 * mm});
            skCircle(sketch, "E800.MirrorC", {"center": v(-11.3, -14.35) * mm, "radius": 0.25 * mm});
            skCircle(sketch, "E801.MirrorC", {"center": v(-13.75, -0.54) * mm, "radius": 0.25 * mm});
            skCircle(sketch, "E802.MirrorC", {"center": v(-10.4, -9.44) * mm, "radius": 0.25 * mm});
            skCircle(sketch, "E803.MirrorC", {"center": v(-2.47, -9.57) * mm, "radius": 0.25 * mm});
            skCircle(sketch, "E804.MirrorC", {"center": v(-1.86, -8.58) * mm, "radius": 0.25 * mm});
            skCircle(sketch, "E805.MirrorC", {"center": v(-8.93, -20.33) * mm, "radius": 0.25 * mm});
            skCircle(sketch, "E806.MirrorC", {"center": v(-12.06, -1.6) * mm, "radius": 0.25 * mm});
            skCircle(sketch, "E807.MirrorC", {"center": v(-4.06, -8.57) * mm, "radius": 0.25 * mm});
            skCircle(sketch, "E808.MirrorC", {"center": v(-12.09, -23.29) * mm, "radius": 0.25 * mm});
            skCircle(sketch, "E809.MirrorC", {"center": v(-4.14, -17.36) * mm, "radius": 0.25 * mm});
            skCircle(sketch, "E810.MirrorC", {"center": v(-13.74, -22.21) * mm, "radius": 0.25 * mm});
            skCircle(sketch, "E811.MirrorC", {"center": v(-7.3, -6.52) * mm, "radius": 0.25 * mm});
            skCircle(sketch, "E812.MirrorC", {"center": v(-8.19, -10.44) * mm, "radius": 0.25 * mm});
            skCircle(sketch, "E813.MirrorC", {"center": v(-2.57, -21.37) * mm, "radius": 0.25 * mm});
            skCircle(sketch, "E814.MirrorC", {"center": v(-8.1, -22.3) * mm, "radius": 0.25 * mm});
            skCircle(sketch, "E815.MirrorC", {"center": v(-6.5, -3.58) * mm, "radius": 0.25 * mm});
            skCircle(sketch, "E816.MirrorC", {"center": v(-0.52, -17.38) * mm, "radius": 0.25 * mm});
            skCircle(sketch, "E817.MirrorC", {"center": v(-4.95, -12.45) * mm, "radius": 0.25 * mm});
            skCircle(sketch, "E818.MirrorC", {"center": v(-12.9, -11.35) * mm, "radius": 0.25 * mm});
            skCircle(sketch, "E819.MirrorC", {"center": v(-5.72, -7.55) * mm, "radius": 0.25 * mm});
            skCircle(sketch, "E820.MirrorC", {"center": v(-0.44, -6.6) * mm, "radius": 0.25 * mm});
            skCircle(sketch, "E821.MirrorC", {"center": v(-2.54, -14.45) * mm, "radius": 0.25 * mm});
            skCircle(sketch, "E822.MirrorC", {"center": v(-8.19, -15.38) * mm, "radius": 0.25 * mm});
            skCircle(sketch, "E823.MirrorC", {"center": v(-11.41, -10.39) * mm, "radius": 0.25 * mm});
            skCircle(sketch, "E824.MirrorC", {"center": v(-5.8, -12.43) * mm, "radius": 0.25 * mm});
            skCircle(sketch, "E825.MirrorC", {"center": v(-0.52, -11.47) * mm, "radius": 0.25 * mm});
            skCircle(sketch, "E826.MirrorC", {"center": v(-8.11, -5.56) * mm, "radius": 0.25 * mm});
            skCircle(sketch, "E827.MirrorC", {"center": v(-12.82, -3.53) * mm, "radius": 0.25 * mm});
            skCircle(sketch, "E828.MirrorC", {"center": v(-1.93, -18.4) * mm, "radius": 0.25 * mm});
            skCircle(sketch, "E829.MirrorC", {"center": v(-1.78, -9.55) * mm, "radius": 0.25 * mm});
            skCircle(sketch, "E830.MirrorC", {"center": v(-10.52, -0.54) * mm, "radius": 0.25 * mm});
            skCircle(sketch, "E831.MirrorC", {"center": v(-10.51, -21.24) * mm, "radius": 0.25 * mm});
            skCircle(sketch, "E832.MirrorC", {"center": v(-13.74, -23.24) * mm, "radius": 0.25 * mm});
            skCircle(sketch, "E833.MirrorC", {"center": v(-10.44, -24.21) * mm, "radius": 0.25 * mm});
            skCircle(sketch, "E834.MirrorC", {"center": v(-13.83, -15.3) * mm, "radius": 0.25 * mm});
            skCircle(sketch, "E835.MirrorC", {"center": v(-0.52, -16.4) * mm, "radius": 0.25 * mm});
            skCircle(sketch, "E836.MirrorC", {"center": v(-4.88, -8.6) * mm, "radius": 0.25 * mm});
            skCircle(sketch, "E837.MirrorC", {"center": v(-8.86, -14.4) * mm, "radius": 0.25 * mm});
            skCircle(sketch, "E838.MirrorC", {"center": v(-8.89, -21.32) * mm, "radius": 0.25 * mm});
            skCircle(sketch, "E839.MirrorC", {"center": v(-4.14, -20.35) * mm, "radius": 0.25 * mm});
            skCircle(sketch, "E840.MirrorC", {"center": v(-10.51, -22.21) * mm, "radius": 0.25 * mm});
            skCircle(sketch, "E841.MirrorC", {"center": v(-1.1, -14.45) * mm, "radius": 0.25 * mm});
            skCircle(sketch, "E842.MirrorC", {"center": v(-7.37, -13.4) * mm, "radius": 0.25 * mm});
            skCircle(sketch, "E843.MirrorC", {"center": v(-6.5, -7.5) * mm, "radius": 0.25 * mm});
            skCircle(sketch, "E844.MirrorC", {"center": v(-8.07, -1.62) * mm, "radius": 0.25 * mm});
            skCircle(sketch, "E845.MirrorC", {"center": v(-14.52, -2.54) * mm, "radius": 0.25 * mm});
            skCircle(sketch, "E846.MirrorC", {"center": v(-1.93, -20.35) * mm, "radius": 0.25 * mm});
            skCircle(sketch, "E847.MirrorC", {"center": v(-5.72, -8.57) * mm, "radius": 0.25 * mm});
            skCircle(sketch, "E848.MirrorC", {"center": v(-1.13, -22.34) * mm, "radius": 0.25 * mm});
            skCircle(sketch, "E849.MirrorC", {"center": v(-13.75, -5.48) * mm, "radius": 0.25 * mm});
            skCircle(sketch, "E850.MirrorC", {"center": v(-3.34, -0.62) * mm, "radius": 0.25 * mm});
            skCircle(sketch, "E851.MirrorC", {"center": v(-9.57, -9.47) * mm, "radius": 0.25 * mm});
            skCircle(sketch, "E852.MirrorC", {"center": v(-1.93, -13.46) * mm, "radius": 0.25 * mm});
            skCircle(sketch, "E853.MirrorC", {"center": v(-8.9, -0.62) * mm, "radius": 0.25 * mm});
            skCircle(sketch, "E854.MirrorC", {"center": v(-6.58, -16.34) * mm, "radius": 0.25 * mm});
            skCircle(sketch, "E855.MirrorC", {"center": v(-10.56, -12.33) * mm, "radius": 0.25 * mm});
            skCircle(sketch, "E856.MirrorC", {"center": v(-8.03, -24.29) * mm, "radius": 0.25 * mm});
            skCircle(sketch, "E857.MirrorC", {"center": v(-3.38, -20.32) * mm, "radius": 0.25 * mm});
            skCircle(sketch, "E858.MirrorC", {"center": v(-6.5, -8.52) * mm, "radius": 0.25 * mm});
            skCircle(sketch, "E859.MirrorC", {"center": v(-1.1, -7.57) * mm, "radius": 0.25 * mm});
            skCircle(sketch, "E860.MirrorC", {"center": v(-11.33, -22.24) * mm, "radius": 0.25 * mm});
            skCircle(sketch, "E861.MirrorC", {"center": v(-8.1, -23.31) * mm, "radius": 0.25 * mm});
            skCircle(sketch, "E862.MirrorC", {"center": v(-3.3, -19.33) * mm, "radius": 0.25 * mm});
            skCircle(sketch, "E863.MirrorC", {"center": v(-4.14, -18.38) * mm, "radius": 0.25 * mm});
            skCircle(sketch, "E864.MirrorC", {"center": v(-9.6, -24.24) * mm, "radius": 0.25 * mm});
            skCircle(sketch, "E865.MirrorC", {"center": v(-3.3, -14.4) * mm, "radius": 0.25 * mm});
            skCircle(sketch, "E866.MirrorC", {"center": v(-4.14, -13.45) * mm, "radius": 0.25 * mm});
            skCircle(sketch, "E867.MirrorC", {"center": v(-7.37, -18.33) * mm, "radius": 0.25 * mm});
            skCircle(sketch, "E868.MirrorC", {"center": v(-9.64, -19.29) * mm, "radius": 0.25 * mm});
            skCircle(sketch, "E869.MirrorC", {"center": v(-3.23, -9.52) * mm, "radius": 0.25 * mm});
            skCircle(sketch, "E870.MirrorC", {"center": v(-4.88, -3.66) * mm, "radius": 0.25 * mm});
            skCircle(sketch, "E871.MirrorC", {"center": v(-12.82, -2.51) * mm, "radius": 0.25 * mm});
            skCircle(sketch, "E872.MirrorC", {"center": v(-12.06, -2.56) * mm, "radius": 0.25 * mm});
            skCircle(sketch, "E873.MirrorC", {"center": v(-8.78, -9.52) * mm, "radius": 0.25 * mm});
            skCircle(sketch, "E874.MirrorC", {"center": v(-11.34, -0.57) * mm, "radius": 0.25 * mm});
            skCircle(sketch, "E875.MirrorC", {"center": v(-14.52, -6.5) * mm, "radius": 0.25 * mm});
            skCircle(sketch, "E876.MirrorC", {"center": v(-9.64, -14.35) * mm, "radius": 0.25 * mm});
            skCircle(sketch, "E877.MirrorC", {"center": v(-3.99, -9.54) * mm, "radius": 0.25 * mm});
            skCircle(sketch, "E878.MirrorC", {"center": v(-7.36, -20.3) * mm, "radius": 0.25 * mm});
            skCircle(sketch, "E879.MirrorC", {"center": v(-1.13, -21.37) * mm, "radius": 0.25 * mm});
            skCircle(sketch, "E880.MirrorC", {"center": v(-5.79, -20.35) * mm, "radius": 0.25 * mm});
            skCircle(sketch, "E881.MirrorC", {"center": v(-13.79, -16.3) * mm, "radius": 0.25 * mm});
            skCircle(sketch, "E882.MirrorC", {"center": v(-7.32, -21.29) * mm, "radius": 0.25 * mm});
            skCircle(sketch, "E883.MirrorC", {"center": v(-11.33, -23.26) * mm, "radius": 0.25 * mm});
            skCircle(sketch, "E884.MirrorC", {"center": v(-7.22, -9.5) * mm, "radius": 0.25 * mm});
            skCircle(sketch, "E885.MirrorC", {"center": v(-6.5, -2.56) * mm, "radius": 0.25 * mm});
            skCircle(sketch, "E886.MirrorC", {"center": v(-3.23, -4.58) * mm, "radius": 0.25 * mm});
            skCircle(sketch, "E887.MirrorC", {"center": v(-4.06, -3.63) * mm, "radius": 0.25 * mm});
            skCircle(sketch, "E888.MirrorC", {"center": v(-7.3, -8.52) * mm, "radius": 0.25 * mm});
            skCircle(sketch, "E889.MirrorC", {"center": v(-1.03, -9.57) * mm, "radius": 0.25 * mm});
            skCircle(sketch, "E890.MirrorC", {"center": v(-11.25, -24.24) * mm, "radius": 0.25 * mm});
            skCircle(sketch, "E891.MirrorC", {"center": v(-10.48, -19.26) * mm, "radius": 0.25 * mm});
            skCircle(sketch, "E892.MirrorC", {"center": v(-13.83, -10.36) * mm, "radius": 0.25 * mm});
            skCircle(sketch, "E893.MirrorC", {"center": v(-2.54, -19.39) * mm, "radius": 0.25 * mm});
            skCircle(sketch, "E894.MirrorC", {"center": v(-5.8, -18.38) * mm, "radius": 0.25 * mm});
            skCircle(sketch, "E895.MirrorC", {"center": v(-12.9, -16.3) * mm, "radius": 0.25 * mm});
            skCircle(sketch, "E896.MirrorC", {"center": v(-4.95, -17.39) * mm, "radius": 0.25 * mm});
            skCircle(sketch, "E897.MirrorC", {"center": v(-12.17, -15.35) * mm, "radius": 0.25 * mm});
            skCircle(sketch, "E898.MirrorC", {"center": v(-14.52, -1.56) * mm, "radius": 0.25 * mm});
            skCircle(sketch, "E899.MirrorC", {"center": v(-3.38, -18.36) * mm, "radius": 0.25 * mm});
            skCircle(sketch, "E900.MirrorC", {"center": v(-11.3, -19.29) * mm, "radius": 0.25 * mm});
            skCircle(sketch, "E901.MirrorC", {"center": v(-12.17, -10.41) * mm, "radius": 0.25 * mm});
            skCircle(sketch, "E902.MirrorC", {"center": v(-8.93, -18.36) * mm, "radius": 0.25 * mm});
            skCircle(sketch, "E903.MirrorC", {"center": v(-14.64, -15.32) * mm, "radius": 0.25 * mm});
            skCircle(sketch, "E904.MirrorC", {"center": v(-2.62, -12.45) * mm, "radius": 0.25 * mm});
            skCircle(sketch, "E905.MirrorC", {"center": v(-11.33, -21.27) * mm, "radius": 0.25 * mm});
            skCircle(sketch, "E906.MirrorC", {"center": v(-5.8, -17.36) * mm, "radius": 0.25 * mm});
            skCircle(sketch, "E907.MirrorC", {"center": v(-11.34, -5.5) * mm, "radius": 0.25 * mm});
            skCircle(sketch, "E908.MirrorC", {"center": v(-6.58, -12.37) * mm, "radius": 0.25 * mm});
            skCircle(sketch, "E909.MirrorC", {"center": v(-12.06, -6.53) * mm, "radius": 0.25 * mm});
            skCircle(sketch, "E910.MirrorC", {"center": v(-1.1, -19.39) * mm, "radius": 0.25 * mm});
            skCircle(sketch, "E911.MirrorC", {"center": v(-8.07, -6.55) * mm, "radius": 0.25 * mm});
            skCircle(sketch, "E912.MirrorC", {"center": v(-11.3, -1.56) * mm, "radius": 0.25 * mm});
            skCircle(sketch, "E913.MirrorC", {"center": v(-14.52, -7.47) * mm, "radius": 0.25 * mm});
            skCircle(sketch, "E914.MirrorC", {"center": v(-8.89, -22.3) * mm, "radius": 0.25 * mm});
            skCircle(sketch, "E915.MirrorC", {"center": v(-9.69, -5.5) * mm, "radius": 0.25 * mm});
            skCircle(sketch, "E916.MirrorC", {"center": v(-14.6, -16.32) * mm, "radius": 0.25 * mm});
            skCircle(sketch, "E917.MirrorC", {"center": v(-6.58, -17.31) * mm, "radius": 0.25 * mm});
            skCircle(sketch, "E918.MirrorC", {"center": v(-8.86, -19.34) * mm, "radius": 0.25 * mm});
            skCircle(sketch, "E919.MirrorC", {"center": v(-10.6, -15.3) * mm, "radius": 0.25 * mm});
            skCircle(sketch, "E920.MirrorC", {"center": v(-8.07, -3.61) * mm, "radius": 0.25 * mm});
            skCircle(sketch, "E921.MirrorC", {"center": v(-11.3, -3.56) * mm, "radius": 0.25 * mm});
            skCircle(sketch, "E922.MirrorC", {"center": v(-9.64, -2.54) * mm, "radius": 0.25 * mm});
            skCircle(sketch, "E923.MirrorC", {"center": v(-1.14, -0.67) * mm, "radius": 0.25 * mm});
            skCircle(sketch, "E924.MirrorC", {"center": v(-10.52, -5.48) * mm, "radius": 0.25 * mm});
            skCircle(sketch, "E925.MirrorC", {"center": v(-12.82, -7.45) * mm, "radius": 0.25 * mm});
            skCircle(sketch, "E926.MirrorC", {"center": v(-2.58, -5.6) * mm, "radius": 0.25 * mm});
            skCircle(sketch, "E927.MirrorC", {"center": v(-9.69, -0.57) * mm, "radius": 0.25 * mm});
            skCircle(sketch, "E928.MirrorC", {"center": v(-0.44, -7.56) * mm, "radius": 0.25 * mm});
            skCircle(sketch, "E929.MirrorC", {"center": v(-13.71, -6.47) * mm, "radius": 0.25 * mm});
            skCircle(sketch, "E930.MirrorC", {"center": v(-12.13, -11.4) * mm, "radius": 0.25 * mm});
            skCircle(sketch, "E931.MirrorC", {"center": v(-2.58, -0.67) * mm, "radius": 0.25 * mm});
            skCircle(sketch, "E932.MirrorC", {"center": v(-1.86, -14.43) * mm, "radius": 0.25 * mm});
            skCircle(sketch, "E933.MirrorC", {"center": v(-4.95, -13.47) * mm, "radius": 0.25 * mm});
            skCircle(sketch, "E934.MirrorC", {"center": v(-11.37, -24.95) * mm, "radius": 0.25 * mm});
            skCircle(sketch, "E935.MirrorC", {"center": v(-12.13, -20.3) * mm, "radius": 0.25 * mm});
            skCircle(sketch, "E936.MirrorC", {"center": v(-12.85, -21.24) * mm, "radius": 0.25 * mm});
            skCircle(sketch, "E937.MirrorC", {"center": v(-8.86, -2.59) * mm, "radius": 0.25 * mm});
            skCircle(sketch, "E938.MirrorC", {"center": v(-9.64, -7.47) * mm, "radius": 0.25 * mm});
            skCircle(sketch, "E939.MirrorC", {"center": v(-0.44, -14.44) * mm, "radius": 0.25 * mm});
            skCircle(sketch, "E940.MirrorC", {"center": v(-0.44, -2.63) * mm, "radius": 0.25 * mm});
            skCircle(sketch, "E941.MirrorC", {"center": v(-8.07, -8.55) * mm, "radius": 0.25 * mm});
            skCircle(sketch, "E942.MirrorC", {"center": v(-14.45, -9.47) * mm, "radius": 0.25 * mm});
            skCircle(sketch, "E943.MirrorC", {"center": v(-6.55, -0.6) * mm, "radius": 0.25 * mm});
            skCircle(sketch, "E944.MirrorC", {"center": v(-13.71, -1.54) * mm, "radius": 0.25 * mm});
            skCircle(sketch, "E945.MirrorC", {"center": v(-5.76, -5.58) * mm, "radius": 0.25 * mm});
            skCircle(sketch, "E946.MirrorC", {"center": v(-12.9, -12.33) * mm, "radius": 0.25 * mm});
            skCircle(sketch, "E947.MirrorC", {"center": v(-5.72, -3.63) * mm, "radius": 0.25 * mm});
            skCircle(sketch, "E948.MirrorC", {"center": v(-14.6, -11.38) * mm, "radius": 0.25 * mm});
            skCircle(sketch, "E949.MirrorC", {"center": v(-9.67, -21.27) * mm, "radius": 0.25 * mm});
            skCircle(sketch, "E950.MirrorC", {"center": v(-10.48, -14.32) * mm, "radius": 0.25 * mm});
            skCircle(sketch, "E951.MirrorC", {"center": v(-4.06, -1.64) * mm, "radius": 0.25 * mm});
            skCircle(sketch, "E952.MirrorC", {"center": v(-3.3, -2.58) * mm, "radius": 0.25 * mm});
            skCircle(sketch, "E953.MirrorC", {"center": v(-1.93, -11.46) * mm, "radius": 0.25 * mm});
            skCircle(sketch, "E954.MirrorC", {"center": v(-8.11, -0.62) * mm, "radius": 0.25 * mm});
            skCircle(sketch, "E955.MirrorC", {"center": v(-3.33, -21.31) * mm, "radius": 0.25 * mm});
            skPoint(sketch, "E956.0", {"position": v(-1.46, -24.04) * mm});
            skSolve(sketch);
        }
        {
            var Q0;
            Q0 = qSketchRegion(id + "F6", true);
            extrude(context, id + "F7", {"entities" : qUnion([Q0]), "operationType" : NewBodyOperationType.ADD, "oppositeDirection" : true, "depth" : 40 * mm});
        }
    });
